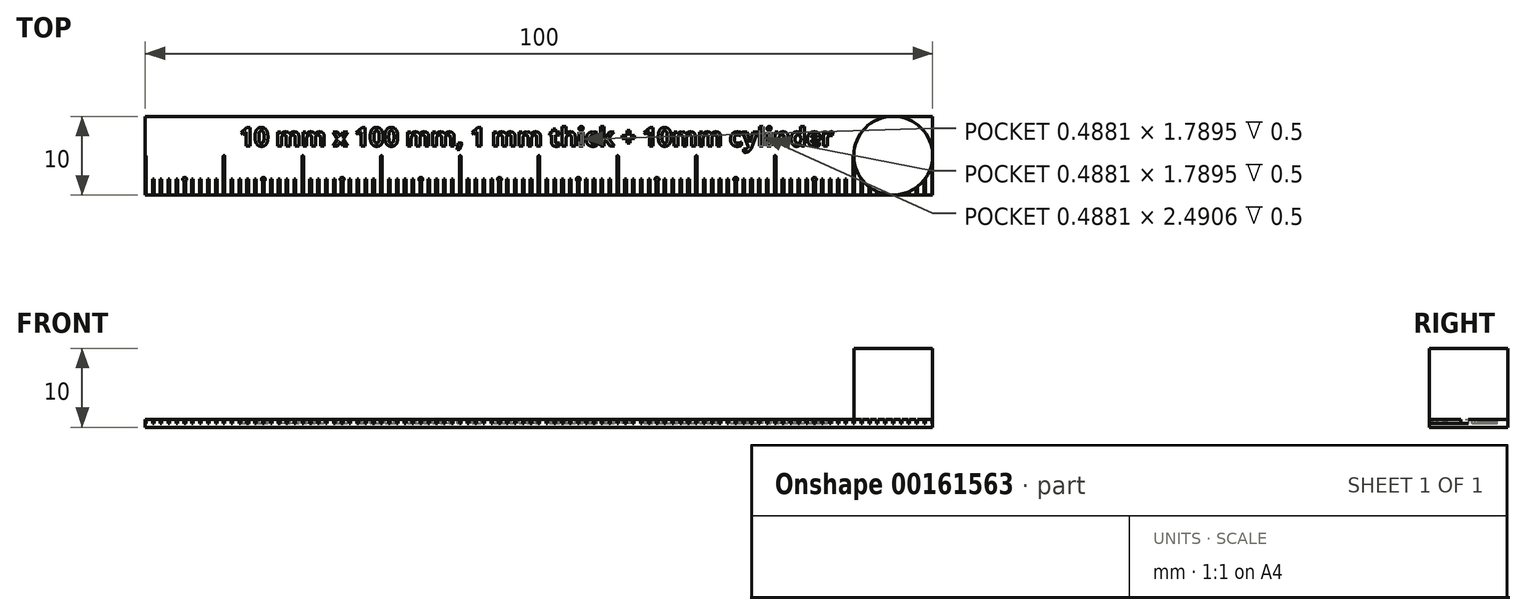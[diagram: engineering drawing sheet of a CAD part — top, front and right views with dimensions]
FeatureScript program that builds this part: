
annotation { "Feature Type Name" : "Feature", "Feature Type Description" : "" }
export const myFeature = defineFeature(function(context is Context, id is Id, definition is map)
    precondition{}
    {
        {
            var Q0;
            Q0=qCreatedBy(makeId("Top.planeOp"),FACE);
            var sketch = newSketch(context, id + "F0", { "sketchPlane" : qUnion([Q0])});
            skLineSegment(sketch, "E0.bottom", {"start": v(50, -5) * mm, "end": v(-50, -5) * mm});
            skLineSegment(sketch, "E0.top", {"start": v(50, 5) * mm, "end": v(-50, 5) * mm});
            skLineSegment(sketch, "E0.left", {"start": v(50, -5) * mm, "end": v(50, 5) * mm});
            skLineSegment(sketch, "E0.right", {"start": v(-50, -5) * mm, "end": v(-50, 5) * mm});
            skPoint(sketch, "E0.middle", {"position": v(0, 0) * mm});
            skSolve(sketch);
        }
        {
            var Q0;
            Q0=makeQuery(id+"F0.imprint","IMPRINT",FACE,{"disambiguationData":[TD([[makeQuery(id+"F0.imprint","IMPRINT",EDGE,{"derivedFrom":sQuery(id+"F0.wireOp",EDGE,"E0.bottom")}),-1.0]])]});
            extrude(context, id + "F1", {"entities" : qUnion([Q0]), "depth" : .5 * mm});
        }
        {
            var Q0;
            Q0=makeQuery(id+"F1.opExtrude","CAP_FACE",FACE,{"disambiguationData":[OSD([sQuery(id+"F0.wireOp",EDGE,"E0.bottom"),sQuery(id+"F0.wireOp",EDGE,"E0.top"),sQuery(id+"F0.wireOp",EDGE,"E0.left"),sQuery(id+"F0.wireOp",EDGE,"E0.right")])],"isStart":false});
            var sketch = newSketch(context, id + "F2", { "sketchPlane" : qUnion([Q0])});
            skLineSegment(sketch, "E1.bottom", {"start": v(-49.9, -5) * mm, "end": v(-50.1, -5) * mm});
            skLineSegment(sketch, "E1.top", {"start": v(-49.9, -0.1) * mm, "end": v(-50.1, -0.1) * mm});
            skLineSegment(sketch, "E1.left", {"start": v(-49.9, -5) * mm, "end": v(-49.9, -0.1) * mm});
            skLineSegment(sketch, "E1.right", {"start": v(-50.1, -5) * mm, "end": v(-50.1, -0.1) * mm});
            skPoint(sketch, "E1.middle", {"position": v(-50, -2.55) * mm});
            skArc(sketch, "E2", {"start": v(-49.9, -0.1) * mm, "mid": v(-50, 0) * mm, "end": v(-50.1, -0.1) * mm});
            skLineSegment(sketch, "E3.bottom", {"start": v(-49.1, -3) * mm, "end": v(-48.9, -3) * mm});
            skLineSegment(sketch, "E3.top", {"start": v(-49.1, -5) * mm, "end": v(-48.9, -5) * mm});
            skLineSegment(sketch, "E3.left", {"start": v(-49.1, -3) * mm, "end": v(-49.1, -5) * mm});
            skLineSegment(sketch, "E3.right", {"start": v(-48.9, -3) * mm, "end": v(-48.9, -5) * mm});
            skPoint(sketch, "E3.middle", {"position": v(-49, -4) * mm});
            skLineSegment(sketch, "E4.1.0.0", {"start": v(-48.1, -3) * mm, "end": v(-47.9, -3) * mm});
            skLineSegment(sketch, "E4.1.0.1", {"start": v(-48.1, -5) * mm, "end": v(-47.9, -5) * mm});
            skPoint(sketch, "E4.1.0.2", {"position": v(-48, -4) * mm});
            skLineSegment(sketch, "E4.1.0.3", {"start": v(-47.9, -3) * mm, "end": v(-47.9, -5) * mm});
            skLineSegment(sketch, "E4.1.0.4", {"start": v(-48.1, -3) * mm, "end": v(-48.1, -5) * mm});
            skLineSegment(sketch, "E4.2.0.0", {"start": v(-47.1, -3) * mm, "end": v(-46.9, -3) * mm});
            skLineSegment(sketch, "E4.2.0.1", {"start": v(-47.1, -5) * mm, "end": v(-46.9, -5) * mm});
            skPoint(sketch, "E4.2.0.2", {"position": v(-47, -4) * mm});
            skLineSegment(sketch, "E4.2.0.3", {"start": v(-46.9, -3) * mm, "end": v(-46.9, -5) * mm});
            skLineSegment(sketch, "E4.2.0.4", {"start": v(-47.1, -3) * mm, "end": v(-47.1, -5) * mm});
            skLineSegment(sketch, "E4.3.0.0", {"start": v(-46.1, -3) * mm, "end": v(-45.9, -3) * mm});
            skLineSegment(sketch, "E4.3.0.1", {"start": v(-46.1, -5) * mm, "end": v(-45.9, -5) * mm});
            skPoint(sketch, "E4.3.0.2", {"position": v(-46, -4) * mm});
            skLineSegment(sketch, "E4.3.0.3", {"start": v(-45.9, -3) * mm, "end": v(-45.9, -5) * mm});
            skLineSegment(sketch, "E4.3.0.4", {"start": v(-46.1, -3) * mm, "end": v(-46.1, -5) * mm});
            skLineSegment(sketch, "E4.4.0.0", {"start": v(-45.1, -3) * mm, "end": v(-44.9, -3) * mm});
            skLineSegment(sketch, "E4.4.0.1", {"start": v(-45.1, -5) * mm, "end": v(-44.9, -5) * mm});
            skPoint(sketch, "E4.4.0.2", {"position": v(-45, -4) * mm});
            skLineSegment(sketch, "E4.4.0.3", {"start": v(-44.9, -3) * mm, "end": v(-44.9, -5) * mm});
            skLineSegment(sketch, "E4.4.0.4", {"start": v(-45.1, -3) * mm, "end": v(-45.1, -5) * mm});
            skLineSegment(sketch, "E4.5.0.0", {"start": v(-44.1, -3) * mm, "end": v(-43.9, -3) * mm});
            skLineSegment(sketch, "E4.5.0.1", {"start": v(-44.1, -5) * mm, "end": v(-43.9, -5) * mm});
            skPoint(sketch, "E4.5.0.2", {"position": v(-44, -4) * mm});
            skLineSegment(sketch, "E4.5.0.3", {"start": v(-43.9, -3) * mm, "end": v(-43.9, -5) * mm});
            skLineSegment(sketch, "E4.5.0.4", {"start": v(-44.1, -3) * mm, "end": v(-44.1, -5) * mm});
            skLineSegment(sketch, "E4.6.0.0", {"start": v(-43.1, -3) * mm, "end": v(-42.9, -3) * mm});
            skLineSegment(sketch, "E4.6.0.1", {"start": v(-43.1, -5) * mm, "end": v(-42.9, -5) * mm});
            skPoint(sketch, "E4.6.0.2", {"position": v(-43, -4) * mm});
            skLineSegment(sketch, "E4.6.0.3", {"start": v(-42.9, -3) * mm, "end": v(-42.9, -5) * mm});
            skLineSegment(sketch, "E4.6.0.4", {"start": v(-43.1, -3) * mm, "end": v(-43.1, -5) * mm});
            skLineSegment(sketch, "E4.7.0.0", {"start": v(-42.1, -3) * mm, "end": v(-41.9, -3) * mm});
            skLineSegment(sketch, "E4.7.0.1", {"start": v(-42.1, -5) * mm, "end": v(-41.9, -5) * mm});
            skPoint(sketch, "E4.7.0.2", {"position": v(-42, -4) * mm});
            skLineSegment(sketch, "E4.7.0.3", {"start": v(-41.9, -3) * mm, "end": v(-41.9, -5) * mm});
            skLineSegment(sketch, "E4.7.0.4", {"start": v(-42.1, -3) * mm, "end": v(-42.1, -5) * mm});
            skLineSegment(sketch, "E4.8.0.0", {"start": v(-41.1, -3) * mm, "end": v(-40.9, -3) * mm});
            skLineSegment(sketch, "E4.8.0.1", {"start": v(-41.1, -5) * mm, "end": v(-40.9, -5) * mm});
            skPoint(sketch, "E4.8.0.2", {"position": v(-41, -4) * mm});
            skLineSegment(sketch, "E4.8.0.3", {"start": v(-40.9, -3) * mm, "end": v(-40.9, -5) * mm});
            skLineSegment(sketch, "E4.8.0.4", {"start": v(-41.1, -3) * mm, "end": v(-41.1, -5) * mm});
            skLineSegment(sketch, "E4.direction1", {"start": v(-49.1, -5) * mm, "end": v(-48.1, -5) * mm, "construction": true});
            skCircle(sketch, "E5", {"center": v(-45, -3) * mm, "radius": 0.25 * mm});
            skPoint(sketch, "E6.1.0.0", {"position": v(-36, -4) * mm});
            skPoint(sketch, "E6.1.0.1", {"position": v(-40, -2.55) * mm});
            skPoint(sketch, "E6.1.0.2", {"position": v(-35, -4) * mm});
            skLineSegment(sketch, "E6.1.0.3", {"start": v(-40.1, -5) * mm, "end": v(-40.1, -0.1) * mm});
            skPoint(sketch, "E6.1.0.4", {"position": v(-39, -4) * mm});
            skPoint(sketch, "E6.1.0.5", {"position": v(-37, -4) * mm});
            skPoint(sketch, "E6.1.0.6", {"position": v(-33, -4) * mm});
            skPoint(sketch, "E6.1.0.7", {"position": v(-31, -4) * mm});
            skPoint(sketch, "E6.1.0.8", {"position": v(-34, -4) * mm});
            skPoint(sketch, "E6.1.0.9", {"position": v(-38, -4) * mm});
            skPoint(sketch, "E6.1.0.10", {"position": v(-32, -4) * mm});
            skLineSegment(sketch, "E6.1.0.11", {"start": v(-32.9, -3) * mm, "end": v(-32.9, -5) * mm});
            skLineSegment(sketch, "E6.1.0.12", {"start": v(-35.9, -3) * mm, "end": v(-35.9, -5) * mm});
            skLineSegment(sketch, "E6.1.0.13", {"start": v(-31.9, -3) * mm, "end": v(-31.9, -5) * mm});
            skLineSegment(sketch, "E6.1.0.14", {"start": v(-38.1, -3) * mm, "end": v(-38.1, -5) * mm});
            skLineSegment(sketch, "E6.1.0.15", {"start": v(-37.9, -3) * mm, "end": v(-37.9, -5) * mm});
            skLineSegment(sketch, "E6.1.0.16", {"start": v(-38.9, -3) * mm, "end": v(-38.9, -5) * mm});
            skLineSegment(sketch, "E6.1.0.17", {"start": v(-39.1, -3) * mm, "end": v(-39.1, -5) * mm});
            skLineSegment(sketch, "E6.1.0.18", {"start": v(-39.9, -5) * mm, "end": v(-39.9, -0.1) * mm});
            skLineSegment(sketch, "E6.1.0.19", {"start": v(-36.9, -3) * mm, "end": v(-36.9, -5) * mm});
            skLineSegment(sketch, "E6.1.0.20", {"start": v(-34.1, -3) * mm, "end": v(-34.1, -5) * mm});
            skLineSegment(sketch, "E6.1.0.21", {"start": v(-31.1, -3) * mm, "end": v(-31.1, -5) * mm});
            skLineSegment(sketch, "E6.1.0.22", {"start": v(-35.1, -3) * mm, "end": v(-35.1, -5) * mm});
            skLineSegment(sketch, "E6.1.0.23", {"start": v(-37.1, -3) * mm, "end": v(-37.1, -5) * mm});
            skLineSegment(sketch, "E6.1.0.24", {"start": v(-33.1, -3) * mm, "end": v(-33.1, -5) * mm});
            skLineSegment(sketch, "E6.1.0.25", {"start": v(-36.1, -3) * mm, "end": v(-36.1, -5) * mm});
            skLineSegment(sketch, "E6.1.0.26", {"start": v(-32.1, -3) * mm, "end": v(-32.1, -5) * mm});
            skLineSegment(sketch, "E6.1.0.27", {"start": v(-34.9, -3) * mm, "end": v(-34.9, -5) * mm});
            skLineSegment(sketch, "E6.1.0.28", {"start": v(-30.9, -3) * mm, "end": v(-30.9, -5) * mm});
            skLineSegment(sketch, "E6.1.0.29", {"start": v(-33.9, -3) * mm, "end": v(-33.9, -5) * mm});
            skLineSegment(sketch, "E6.1.0.30", {"start": v(-38.1, -3) * mm, "end": v(-37.9, -3) * mm});
            skLineSegment(sketch, "E6.1.0.31", {"start": v(-39.1, -3) * mm, "end": v(-38.9, -3) * mm});
            skLineSegment(sketch, "E6.1.0.32", {"start": v(-36.1, -3) * mm, "end": v(-35.9, -3) * mm});
            skLineSegment(sketch, "E6.1.0.33", {"start": v(-32.1, -3) * mm, "end": v(-31.9, -3) * mm});
            skLineSegment(sketch, "E6.1.0.34", {"start": v(-31.1, -3) * mm, "end": v(-30.9, -3) * mm});
            skLineSegment(sketch, "E6.1.0.35", {"start": v(-31.1, -5) * mm, "end": v(-30.9, -5) * mm});
            skLineSegment(sketch, "E6.1.0.36", {"start": v(-32.1, -5) * mm, "end": v(-31.9, -5) * mm});
            skLineSegment(sketch, "E6.1.0.37", {"start": v(-35.1, -5) * mm, "end": v(-34.9, -5) * mm});
            skLineSegment(sketch, "E6.1.0.38", {"start": v(-36.1, -5) * mm, "end": v(-35.9, -5) * mm});
            skLineSegment(sketch, "E6.1.0.39", {"start": v(-34.1, -5) * mm, "end": v(-33.9, -5) * mm});
            skLineSegment(sketch, "E6.1.0.40", {"start": v(-34.1, -3) * mm, "end": v(-33.9, -3) * mm});
            skLineSegment(sketch, "E6.1.0.41", {"start": v(-39.9, -5) * mm, "end": v(-40.1, -5) * mm});
            skLineSegment(sketch, "E6.1.0.42", {"start": v(-37.1, -5) * mm, "end": v(-36.9, -5) * mm});
            skLineSegment(sketch, "E6.1.0.43", {"start": v(-37.1, -3) * mm, "end": v(-36.9, -3) * mm});
            skLineSegment(sketch, "E6.1.0.44", {"start": v(-33.1, -5) * mm, "end": v(-32.9, -5) * mm});
            skLineSegment(sketch, "E6.1.0.45", {"start": v(-33.1, -3) * mm, "end": v(-32.9, -3) * mm});
            skCircle(sketch, "E6.1.0.46", {"center": v(-35, -3) * mm, "radius": 0.25 * mm});
            skLineSegment(sketch, "E6.1.0.47", {"start": v(-39.1, -5) * mm, "end": v(-38.1, -5) * mm, "construction": true});
            skLineSegment(sketch, "E6.1.0.48", {"start": v(-38.1, -5) * mm, "end": v(-37.9, -5) * mm});
            skLineSegment(sketch, "E6.1.0.49", {"start": v(-39.1, -5) * mm, "end": v(-38.9, -5) * mm});
            skLineSegment(sketch, "E6.1.0.50", {"start": v(-35.1, -3) * mm, "end": v(-34.9, -3) * mm});
            skArc(sketch, "E6.1.0.51", {"start": v(-39.9, -0.1) * mm, "mid": v(-40, 0) * mm, "end": v(-40.1, -0.1) * mm});
            skLineSegment(sketch, "E6.1.0.52", {"start": v(-39.9, -0.1) * mm, "end": v(-40.1, -0.1) * mm});
            skPoint(sketch, "E6.2.0.0", {"position": v(-26, -4) * mm});
            skPoint(sketch, "E6.2.0.1", {"position": v(-30, -2.55) * mm});
            skPoint(sketch, "E6.2.0.2", {"position": v(-25, -4) * mm});
            skLineSegment(sketch, "E6.2.0.3", {"start": v(-30.1, -5) * mm, "end": v(-30.1, -0.1) * mm});
            skPoint(sketch, "E6.2.0.4", {"position": v(-29, -4) * mm});
            skPoint(sketch, "E6.2.0.5", {"position": v(-27, -4) * mm});
            skPoint(sketch, "E6.2.0.6", {"position": v(-23, -4) * mm});
            skPoint(sketch, "E6.2.0.7", {"position": v(-21, -4) * mm});
            skPoint(sketch, "E6.2.0.8", {"position": v(-24, -4) * mm});
            skPoint(sketch, "E6.2.0.9", {"position": v(-28, -4) * mm});
            skPoint(sketch, "E6.2.0.10", {"position": v(-22, -4) * mm});
            skLineSegment(sketch, "E6.2.0.11", {"start": v(-22.9, -3) * mm, "end": v(-22.9, -5) * mm});
            skLineSegment(sketch, "E6.2.0.12", {"start": v(-25.9, -3) * mm, "end": v(-25.9, -5) * mm});
            skLineSegment(sketch, "E6.2.0.13", {"start": v(-21.9, -3) * mm, "end": v(-21.9, -5) * mm});
            skLineSegment(sketch, "E6.2.0.14", {"start": v(-28.1, -3) * mm, "end": v(-28.1, -5) * mm});
            skLineSegment(sketch, "E6.2.0.15", {"start": v(-27.9, -3) * mm, "end": v(-27.9, -5) * mm});
            skLineSegment(sketch, "E6.2.0.16", {"start": v(-28.9, -3) * mm, "end": v(-28.9, -5) * mm});
            skLineSegment(sketch, "E6.2.0.17", {"start": v(-29.1, -3) * mm, "end": v(-29.1, -5) * mm});
            skLineSegment(sketch, "E6.2.0.18", {"start": v(-29.9, -5) * mm, "end": v(-29.9, -0.1) * mm});
            skLineSegment(sketch, "E6.2.0.19", {"start": v(-26.9, -3) * mm, "end": v(-26.9, -5) * mm});
            skLineSegment(sketch, "E6.2.0.20", {"start": v(-24.1, -3) * mm, "end": v(-24.1, -5) * mm});
            skLineSegment(sketch, "E6.2.0.21", {"start": v(-21.1, -3) * mm, "end": v(-21.1, -5) * mm});
            skLineSegment(sketch, "E6.2.0.22", {"start": v(-25.1, -3) * mm, "end": v(-25.1, -5) * mm});
            skLineSegment(sketch, "E6.2.0.23", {"start": v(-27.1, -3) * mm, "end": v(-27.1, -5) * mm});
            skLineSegment(sketch, "E6.2.0.24", {"start": v(-23.1, -3) * mm, "end": v(-23.1, -5) * mm});
            skLineSegment(sketch, "E6.2.0.25", {"start": v(-26.1, -3) * mm, "end": v(-26.1, -5) * mm});
            skLineSegment(sketch, "E6.2.0.26", {"start": v(-22.1, -3) * mm, "end": v(-22.1, -5) * mm});
            skLineSegment(sketch, "E6.2.0.27", {"start": v(-24.9, -3) * mm, "end": v(-24.9, -5) * mm});
            skLineSegment(sketch, "E6.2.0.28", {"start": v(-20.9, -3) * mm, "end": v(-20.9, -5) * mm});
            skLineSegment(sketch, "E6.2.0.29", {"start": v(-23.9, -3) * mm, "end": v(-23.9, -5) * mm});
            skLineSegment(sketch, "E6.2.0.30", {"start": v(-28.1, -3) * mm, "end": v(-27.9, -3) * mm});
            skLineSegment(sketch, "E6.2.0.31", {"start": v(-29.1, -3) * mm, "end": v(-28.9, -3) * mm});
            skLineSegment(sketch, "E6.2.0.32", {"start": v(-26.1, -3) * mm, "end": v(-25.9, -3) * mm});
            skLineSegment(sketch, "E6.2.0.33", {"start": v(-22.1, -3) * mm, "end": v(-21.9, -3) * mm});
            skLineSegment(sketch, "E6.2.0.34", {"start": v(-21.1, -3) * mm, "end": v(-20.9, -3) * mm});
            skLineSegment(sketch, "E6.2.0.35", {"start": v(-21.1, -5) * mm, "end": v(-20.9, -5) * mm});
            skLineSegment(sketch, "E6.2.0.36", {"start": v(-22.1, -5) * mm, "end": v(-21.9, -5) * mm});
            skLineSegment(sketch, "E6.2.0.37", {"start": v(-25.1, -5) * mm, "end": v(-24.9, -5) * mm});
            skLineSegment(sketch, "E6.2.0.38", {"start": v(-26.1, -5) * mm, "end": v(-25.9, -5) * mm});
            skLineSegment(sketch, "E6.2.0.39", {"start": v(-24.1, -5) * mm, "end": v(-23.9, -5) * mm});
            skLineSegment(sketch, "E6.2.0.40", {"start": v(-24.1, -3) * mm, "end": v(-23.9, -3) * mm});
            skLineSegment(sketch, "E6.2.0.41", {"start": v(-29.9, -5) * mm, "end": v(-30.1, -5) * mm});
            skLineSegment(sketch, "E6.2.0.42", {"start": v(-27.1, -5) * mm, "end": v(-26.9, -5) * mm});
            skLineSegment(sketch, "E6.2.0.43", {"start": v(-27.1, -3) * mm, "end": v(-26.9, -3) * mm});
            skLineSegment(sketch, "E6.2.0.44", {"start": v(-23.1, -5) * mm, "end": v(-22.9, -5) * mm});
            skLineSegment(sketch, "E6.2.0.45", {"start": v(-23.1, -3) * mm, "end": v(-22.9, -3) * mm});
            skCircle(sketch, "E6.2.0.46", {"center": v(-25, -3) * mm, "radius": 0.25 * mm});
            skLineSegment(sketch, "E6.2.0.47", {"start": v(-29.1, -5) * mm, "end": v(-28.1, -5) * mm, "construction": true});
            skLineSegment(sketch, "E6.2.0.48", {"start": v(-28.1, -5) * mm, "end": v(-27.9, -5) * mm});
            skLineSegment(sketch, "E6.2.0.49", {"start": v(-29.1, -5) * mm, "end": v(-28.9, -5) * mm});
            skLineSegment(sketch, "E6.2.0.50", {"start": v(-25.1, -3) * mm, "end": v(-24.9, -3) * mm});
            skArc(sketch, "E6.2.0.51", {"start": v(-29.9, -0.1) * mm, "mid": v(-30, 0) * mm, "end": v(-30.1, -0.1) * mm});
            skLineSegment(sketch, "E6.2.0.52", {"start": v(-29.9, -0.1) * mm, "end": v(-30.1, -0.1) * mm});
            skPoint(sketch, "E6.3.0.0", {"position": v(-16, -4) * mm});
            skPoint(sketch, "E6.3.0.1", {"position": v(-20, -2.55) * mm});
            skPoint(sketch, "E6.3.0.2", {"position": v(-15, -4) * mm});
            skLineSegment(sketch, "E6.3.0.3", {"start": v(-20.1, -5) * mm, "end": v(-20.1, -0.1) * mm});
            skPoint(sketch, "E6.3.0.4", {"position": v(-19, -4) * mm});
            skPoint(sketch, "E6.3.0.5", {"position": v(-17, -4) * mm});
            skPoint(sketch, "E6.3.0.6", {"position": v(-13, -4) * mm});
            skPoint(sketch, "E6.3.0.7", {"position": v(-11, -4) * mm});
            skPoint(sketch, "E6.3.0.8", {"position": v(-14, -4) * mm});
            skPoint(sketch, "E6.3.0.9", {"position": v(-18, -4) * mm});
            skPoint(sketch, "E6.3.0.10", {"position": v(-12, -4) * mm});
            skLineSegment(sketch, "E6.3.0.11", {"start": v(-12.9, -3) * mm, "end": v(-12.9, -5) * mm});
            skLineSegment(sketch, "E6.3.0.12", {"start": v(-15.9, -3) * mm, "end": v(-15.9, -5) * mm});
            skLineSegment(sketch, "E6.3.0.13", {"start": v(-11.9, -3) * mm, "end": v(-11.9, -5) * mm});
            skLineSegment(sketch, "E6.3.0.14", {"start": v(-18.1, -3) * mm, "end": v(-18.1, -5) * mm});
            skLineSegment(sketch, "E6.3.0.15", {"start": v(-17.9, -3) * mm, "end": v(-17.9, -5) * mm});
            skLineSegment(sketch, "E6.3.0.16", {"start": v(-18.9, -3) * mm, "end": v(-18.9, -5) * mm});
            skLineSegment(sketch, "E6.3.0.17", {"start": v(-19.1, -3) * mm, "end": v(-19.1, -5) * mm});
            skLineSegment(sketch, "E6.3.0.18", {"start": v(-19.9, -5) * mm, "end": v(-19.9, -0.1) * mm});
            skLineSegment(sketch, "E6.3.0.19", {"start": v(-16.9, -3) * mm, "end": v(-16.9, -5) * mm});
            skLineSegment(sketch, "E6.3.0.20", {"start": v(-14.1, -3) * mm, "end": v(-14.1, -5) * mm});
            skLineSegment(sketch, "E6.3.0.21", {"start": v(-11.1, -3) * mm, "end": v(-11.1, -5) * mm});
            skLineSegment(sketch, "E6.3.0.22", {"start": v(-15.1, -3) * mm, "end": v(-15.1, -5) * mm});
            skLineSegment(sketch, "E6.3.0.23", {"start": v(-17.1, -3) * mm, "end": v(-17.1, -5) * mm});
            skLineSegment(sketch, "E6.3.0.24", {"start": v(-13.1, -3) * mm, "end": v(-13.1, -5) * mm});
            skLineSegment(sketch, "E6.3.0.25", {"start": v(-16.1, -3) * mm, "end": v(-16.1, -5) * mm});
            skLineSegment(sketch, "E6.3.0.26", {"start": v(-12.1, -3) * mm, "end": v(-12.1, -5) * mm});
            skLineSegment(sketch, "E6.3.0.27", {"start": v(-14.9, -3) * mm, "end": v(-14.9, -5) * mm});
            skLineSegment(sketch, "E6.3.0.28", {"start": v(-10.9, -3) * mm, "end": v(-10.9, -5) * mm});
            skLineSegment(sketch, "E6.3.0.29", {"start": v(-13.9, -3) * mm, "end": v(-13.9, -5) * mm});
            skLineSegment(sketch, "E6.3.0.30", {"start": v(-18.1, -3) * mm, "end": v(-17.9, -3) * mm});
            skLineSegment(sketch, "E6.3.0.31", {"start": v(-19.1, -3) * mm, "end": v(-18.9, -3) * mm});
            skLineSegment(sketch, "E6.3.0.32", {"start": v(-16.1, -3) * mm, "end": v(-15.9, -3) * mm});
            skLineSegment(sketch, "E6.3.0.33", {"start": v(-12.1, -3) * mm, "end": v(-11.9, -3) * mm});
            skLineSegment(sketch, "E6.3.0.34", {"start": v(-11.1, -3) * mm, "end": v(-10.9, -3) * mm});
            skLineSegment(sketch, "E6.3.0.35", {"start": v(-11.1, -5) * mm, "end": v(-10.9, -5) * mm});
            skLineSegment(sketch, "E6.3.0.36", {"start": v(-12.1, -5) * mm, "end": v(-11.9, -5) * mm});
            skLineSegment(sketch, "E6.3.0.37", {"start": v(-15.1, -5) * mm, "end": v(-14.9, -5) * mm});
            skLineSegment(sketch, "E6.3.0.38", {"start": v(-16.1, -5) * mm, "end": v(-15.9, -5) * mm});
            skLineSegment(sketch, "E6.3.0.39", {"start": v(-14.1, -5) * mm, "end": v(-13.9, -5) * mm});
            skLineSegment(sketch, "E6.3.0.40", {"start": v(-14.1, -3) * mm, "end": v(-13.9, -3) * mm});
            skLineSegment(sketch, "E6.3.0.41", {"start": v(-19.9, -5) * mm, "end": v(-20.1, -5) * mm});
            skLineSegment(sketch, "E6.3.0.42", {"start": v(-17.1, -5) * mm, "end": v(-16.9, -5) * mm});
            skLineSegment(sketch, "E6.3.0.43", {"start": v(-17.1, -3) * mm, "end": v(-16.9, -3) * mm});
            skLineSegment(sketch, "E6.3.0.44", {"start": v(-13.1, -5) * mm, "end": v(-12.9, -5) * mm});
            skLineSegment(sketch, "E6.3.0.45", {"start": v(-13.1, -3) * mm, "end": v(-12.9, -3) * mm});
            skCircle(sketch, "E6.3.0.46", {"center": v(-15, -3) * mm, "radius": 0.25 * mm});
            skLineSegment(sketch, "E6.3.0.47", {"start": v(-19.1, -5) * mm, "end": v(-18.1, -5) * mm, "construction": true});
            skLineSegment(sketch, "E6.3.0.48", {"start": v(-18.1, -5) * mm, "end": v(-17.9, -5) * mm});
            skLineSegment(sketch, "E6.3.0.49", {"start": v(-19.1, -5) * mm, "end": v(-18.9, -5) * mm});
            skLineSegment(sketch, "E6.3.0.50", {"start": v(-15.1, -3) * mm, "end": v(-14.9, -3) * mm});
            skArc(sketch, "E6.3.0.51", {"start": v(-19.9, -0.1) * mm, "mid": v(-20, 0) * mm, "end": v(-20.1, -0.1) * mm});
            skLineSegment(sketch, "E6.3.0.52", {"start": v(-19.9, -0.1) * mm, "end": v(-20.1, -0.1) * mm});
            skPoint(sketch, "E6.4.0.0", {"position": v(-6, -4) * mm});
            skPoint(sketch, "E6.4.0.1", {"position": v(-10, -2.55) * mm});
            skPoint(sketch, "E6.4.0.2", {"position": v(-5, -4) * mm});
            skLineSegment(sketch, "E6.4.0.3", {"start": v(-10.1, -5) * mm, "end": v(-10.1, -0.1) * mm});
            skPoint(sketch, "E6.4.0.4", {"position": v(-9, -4) * mm});
            skPoint(sketch, "E6.4.0.5", {"position": v(-7, -4) * mm});
            skPoint(sketch, "E6.4.0.6", {"position": v(-3, -4) * mm});
            skPoint(sketch, "E6.4.0.7", {"position": v(-1, -4) * mm});
            skPoint(sketch, "E6.4.0.8", {"position": v(-4, -4) * mm});
            skPoint(sketch, "E6.4.0.9", {"position": v(-8, -4) * mm});
            skPoint(sketch, "E6.4.0.10", {"position": v(-2, -4) * mm});
            skLineSegment(sketch, "E6.4.0.11", {"start": v(-2.9, -3) * mm, "end": v(-2.9, -5) * mm});
            skLineSegment(sketch, "E6.4.0.12", {"start": v(-5.9, -3) * mm, "end": v(-5.9, -5) * mm});
            skLineSegment(sketch, "E6.4.0.13", {"start": v(-1.9, -3) * mm, "end": v(-1.9, -5) * mm});
            skLineSegment(sketch, "E6.4.0.14", {"start": v(-8.1, -3) * mm, "end": v(-8.1, -5) * mm});
            skLineSegment(sketch, "E6.4.0.15", {"start": v(-7.9, -3) * mm, "end": v(-7.9, -5) * mm});
            skLineSegment(sketch, "E6.4.0.16", {"start": v(-8.9, -3) * mm, "end": v(-8.9, -5) * mm});
            skLineSegment(sketch, "E6.4.0.17", {"start": v(-9.1, -3) * mm, "end": v(-9.1, -5) * mm});
            skLineSegment(sketch, "E6.4.0.18", {"start": v(-9.9, -5) * mm, "end": v(-9.9, -0.1) * mm});
            skLineSegment(sketch, "E6.4.0.19", {"start": v(-6.9, -3) * mm, "end": v(-6.9, -5) * mm});
            skLineSegment(sketch, "E6.4.0.20", {"start": v(-4.1, -3) * mm, "end": v(-4.1, -5) * mm});
            skLineSegment(sketch, "E6.4.0.21", {"start": v(-1.1, -3) * mm, "end": v(-1.1, -5) * mm});
            skLineSegment(sketch, "E6.4.0.22", {"start": v(-5.1, -3) * mm, "end": v(-5.1, -5) * mm});
            skLineSegment(sketch, "E6.4.0.23", {"start": v(-7.1, -3) * mm, "end": v(-7.1, -5) * mm});
            skLineSegment(sketch, "E6.4.0.24", {"start": v(-3.1, -3) * mm, "end": v(-3.1, -5) * mm});
            skLineSegment(sketch, "E6.4.0.25", {"start": v(-6.1, -3) * mm, "end": v(-6.1, -5) * mm});
            skLineSegment(sketch, "E6.4.0.26", {"start": v(-2.1, -3) * mm, "end": v(-2.1, -5) * mm});
            skLineSegment(sketch, "E6.4.0.27", {"start": v(-4.9, -3) * mm, "end": v(-4.9, -5) * mm});
            skLineSegment(sketch, "E6.4.0.28", {"start": v(-0.9, -3) * mm, "end": v(-0.9, -5) * mm});
            skLineSegment(sketch, "E6.4.0.29", {"start": v(-3.9, -3) * mm, "end": v(-3.9, -5) * mm});
            skLineSegment(sketch, "E6.4.0.30", {"start": v(-8.1, -3) * mm, "end": v(-7.9, -3) * mm});
            skLineSegment(sketch, "E6.4.0.31", {"start": v(-9.1, -3) * mm, "end": v(-8.9, -3) * mm});
            skLineSegment(sketch, "E6.4.0.32", {"start": v(-6.1, -3) * mm, "end": v(-5.9, -3) * mm});
            skLineSegment(sketch, "E6.4.0.33", {"start": v(-2.1, -3) * mm, "end": v(-1.9, -3) * mm});
            skLineSegment(sketch, "E6.4.0.34", {"start": v(-1.1, -3) * mm, "end": v(-0.9, -3) * mm});
            skLineSegment(sketch, "E6.4.0.35", {"start": v(-1.1, -5) * mm, "end": v(-0.9, -5) * mm});
            skLineSegment(sketch, "E6.4.0.36", {"start": v(-2.1, -5) * mm, "end": v(-1.9, -5) * mm});
            skLineSegment(sketch, "E6.4.0.37", {"start": v(-5.1, -5) * mm, "end": v(-4.9, -5) * mm});
            skLineSegment(sketch, "E6.4.0.38", {"start": v(-6.1, -5) * mm, "end": v(-5.9, -5) * mm});
            skLineSegment(sketch, "E6.4.0.39", {"start": v(-4.1, -5) * mm, "end": v(-3.9, -5) * mm});
            skLineSegment(sketch, "E6.4.0.40", {"start": v(-4.1, -3) * mm, "end": v(-3.9, -3) * mm});
            skLineSegment(sketch, "E6.4.0.41", {"start": v(-9.9, -5) * mm, "end": v(-10.1, -5) * mm});
            skLineSegment(sketch, "E6.4.0.42", {"start": v(-7.1, -5) * mm, "end": v(-6.9, -5) * mm});
            skLineSegment(sketch, "E6.4.0.43", {"start": v(-7.1, -3) * mm, "end": v(-6.9, -3) * mm});
            skLineSegment(sketch, "E6.4.0.44", {"start": v(-3.1, -5) * mm, "end": v(-2.9, -5) * mm});
            skLineSegment(sketch, "E6.4.0.45", {"start": v(-3.1, -3) * mm, "end": v(-2.9, -3) * mm});
            skCircle(sketch, "E6.4.0.46", {"center": v(-5, -3) * mm, "radius": 0.25 * mm});
            skLineSegment(sketch, "E6.4.0.47", {"start": v(-9.1, -5) * mm, "end": v(-8.1, -5) * mm, "construction": true});
            skLineSegment(sketch, "E6.4.0.48", {"start": v(-8.1, -5) * mm, "end": v(-7.9, -5) * mm});
            skLineSegment(sketch, "E6.4.0.49", {"start": v(-9.1, -5) * mm, "end": v(-8.9, -5) * mm});
            skLineSegment(sketch, "E6.4.0.50", {"start": v(-5.1, -3) * mm, "end": v(-4.9, -3) * mm});
            skArc(sketch, "E6.4.0.51", {"start": v(-9.9, -0.1) * mm, "mid": v(-10, 0) * mm, "end": v(-10.1, -0.1) * mm});
            skLineSegment(sketch, "E6.4.0.52", {"start": v(-9.9, -0.1) * mm, "end": v(-10.1, -0.1) * mm});
            skPoint(sketch, "E6.5.0.0", {"position": v(4, -4) * mm});
            skPoint(sketch, "E6.5.0.1", {"position": v(0, -2.55) * mm});
            skPoint(sketch, "E6.5.0.2", {"position": v(5, -4) * mm});
            skLineSegment(sketch, "E6.5.0.3", {"start": v(-0.1, -5) * mm, "end": v(-0.1, -0.1) * mm});
            skPoint(sketch, "E6.5.0.4", {"position": v(1, -4) * mm});
            skPoint(sketch, "E6.5.0.5", {"position": v(3, -4) * mm});
            skPoint(sketch, "E6.5.0.6", {"position": v(7, -4) * mm});
            skPoint(sketch, "E6.5.0.7", {"position": v(9, -4) * mm});
            skPoint(sketch, "E6.5.0.8", {"position": v(6, -4) * mm});
            skPoint(sketch, "E6.5.0.9", {"position": v(2, -4) * mm});
            skPoint(sketch, "E6.5.0.10", {"position": v(8, -4) * mm});
            skLineSegment(sketch, "E6.5.0.11", {"start": v(7.1, -3) * mm, "end": v(7.1, -5) * mm});
            skLineSegment(sketch, "E6.5.0.12", {"start": v(4.1, -3) * mm, "end": v(4.1, -5) * mm});
            skLineSegment(sketch, "E6.5.0.13", {"start": v(8.1, -3) * mm, "end": v(8.1, -5) * mm});
            skLineSegment(sketch, "E6.5.0.14", {"start": v(1.9, -3) * mm, "end": v(1.9, -5) * mm});
            skLineSegment(sketch, "E6.5.0.15", {"start": v(2.1, -3) * mm, "end": v(2.1, -5) * mm});
            skLineSegment(sketch, "E6.5.0.16", {"start": v(1.1, -3) * mm, "end": v(1.1, -5) * mm});
            skLineSegment(sketch, "E6.5.0.17", {"start": v(0.9, -3) * mm, "end": v(0.9, -5) * mm});
            skLineSegment(sketch, "E6.5.0.18", {"start": v(0.1, -5) * mm, "end": v(0.1, -0.1) * mm});
            skLineSegment(sketch, "E6.5.0.19", {"start": v(3.1, -3) * mm, "end": v(3.1, -5) * mm});
            skLineSegment(sketch, "E6.5.0.20", {"start": v(5.9, -3) * mm, "end": v(5.9, -5) * mm});
            skLineSegment(sketch, "E6.5.0.21", {"start": v(8.9, -3) * mm, "end": v(8.9, -5) * mm});
            skLineSegment(sketch, "E6.5.0.22", {"start": v(4.9, -3) * mm, "end": v(4.9, -5) * mm});
            skLineSegment(sketch, "E6.5.0.23", {"start": v(2.9, -3) * mm, "end": v(2.9, -5) * mm});
            skLineSegment(sketch, "E6.5.0.24", {"start": v(6.9, -3) * mm, "end": v(6.9, -5) * mm});
            skLineSegment(sketch, "E6.5.0.25", {"start": v(3.9, -3) * mm, "end": v(3.9, -5) * mm});
            skLineSegment(sketch, "E6.5.0.26", {"start": v(7.9, -3) * mm, "end": v(7.9, -5) * mm});
            skLineSegment(sketch, "E6.5.0.27", {"start": v(5.1, -3) * mm, "end": v(5.1, -5) * mm});
            skLineSegment(sketch, "E6.5.0.28", {"start": v(9.1, -3) * mm, "end": v(9.1, -5) * mm});
            skLineSegment(sketch, "E6.5.0.29", {"start": v(6.1, -3) * mm, "end": v(6.1, -5) * mm});
            skLineSegment(sketch, "E6.5.0.30", {"start": v(1.9, -3) * mm, "end": v(2.1, -3) * mm});
            skLineSegment(sketch, "E6.5.0.31", {"start": v(0.9, -3) * mm, "end": v(1.1, -3) * mm});
            skLineSegment(sketch, "E6.5.0.32", {"start": v(3.9, -3) * mm, "end": v(4.1, -3) * mm});
            skLineSegment(sketch, "E6.5.0.33", {"start": v(7.9, -3) * mm, "end": v(8.1, -3) * mm});
            skLineSegment(sketch, "E6.5.0.34", {"start": v(8.9, -3) * mm, "end": v(9.1, -3) * mm});
            skLineSegment(sketch, "E6.5.0.35", {"start": v(8.9, -5) * mm, "end": v(9.1, -5) * mm});
            skLineSegment(sketch, "E6.5.0.36", {"start": v(7.9, -5) * mm, "end": v(8.1, -5) * mm});
            skLineSegment(sketch, "E6.5.0.37", {"start": v(4.9, -5) * mm, "end": v(5.1, -5) * mm});
            skLineSegment(sketch, "E6.5.0.38", {"start": v(3.9, -5) * mm, "end": v(4.1, -5) * mm});
            skLineSegment(sketch, "E6.5.0.39", {"start": v(5.9, -5) * mm, "end": v(6.1, -5) * mm});
            skLineSegment(sketch, "E6.5.0.40", {"start": v(5.9, -3) * mm, "end": v(6.1, -3) * mm});
            skLineSegment(sketch, "E6.5.0.41", {"start": v(0.1, -5) * mm, "end": v(-0.1, -5) * mm});
            skLineSegment(sketch, "E6.5.0.42", {"start": v(2.9, -5) * mm, "end": v(3.1, -5) * mm});
            skLineSegment(sketch, "E6.5.0.43", {"start": v(2.9, -3) * mm, "end": v(3.1, -3) * mm});
            skLineSegment(sketch, "E6.5.0.44", {"start": v(6.9, -5) * mm, "end": v(7.1, -5) * mm});
            skLineSegment(sketch, "E6.5.0.45", {"start": v(6.9, -3) * mm, "end": v(7.1, -3) * mm});
            skCircle(sketch, "E6.5.0.46", {"center": v(5, -3) * mm, "radius": 0.25 * mm});
            skLineSegment(sketch, "E6.5.0.47", {"start": v(0.9, -5) * mm, "end": v(1.9, -5) * mm, "construction": true});
            skLineSegment(sketch, "E6.5.0.48", {"start": v(1.9, -5) * mm, "end": v(2.1, -5) * mm});
            skLineSegment(sketch, "E6.5.0.49", {"start": v(0.9, -5) * mm, "end": v(1.1, -5) * mm});
            skLineSegment(sketch, "E6.5.0.50", {"start": v(4.9, -3) * mm, "end": v(5.1, -3) * mm});
            skArc(sketch, "E6.5.0.51", {"start": v(0.1, -0.1) * mm, "mid": v(0, 0) * mm, "end": v(-0.1, -0.1) * mm});
            skLineSegment(sketch, "E6.5.0.52", {"start": v(0.1, -0.1) * mm, "end": v(-0.1, -0.1) * mm});
            skPoint(sketch, "E6.6.0.0", {"position": v(14, -4) * mm});
            skPoint(sketch, "E6.6.0.1", {"position": v(10, -2.55) * mm});
            skPoint(sketch, "E6.6.0.2", {"position": v(15, -4) * mm});
            skLineSegment(sketch, "E6.6.0.3", {"start": v(9.9, -5) * mm, "end": v(9.9, -0.1) * mm});
            skPoint(sketch, "E6.6.0.4", {"position": v(11, -4) * mm});
            skPoint(sketch, "E6.6.0.5", {"position": v(13, -4) * mm});
            skPoint(sketch, "E6.6.0.6", {"position": v(17, -4) * mm});
            skPoint(sketch, "E6.6.0.7", {"position": v(19, -4) * mm});
            skPoint(sketch, "E6.6.0.8", {"position": v(16, -4) * mm});
            skPoint(sketch, "E6.6.0.9", {"position": v(12, -4) * mm});
            skPoint(sketch, "E6.6.0.10", {"position": v(18, -4) * mm});
            skLineSegment(sketch, "E6.6.0.11", {"start": v(17.1, -3) * mm, "end": v(17.1, -5) * mm});
            skLineSegment(sketch, "E6.6.0.12", {"start": v(14.1, -3) * mm, "end": v(14.1, -5) * mm});
            skLineSegment(sketch, "E6.6.0.13", {"start": v(18.1, -3) * mm, "end": v(18.1, -5) * mm});
            skLineSegment(sketch, "E6.6.0.14", {"start": v(11.9, -3) * mm, "end": v(11.9, -5) * mm});
            skLineSegment(sketch, "E6.6.0.15", {"start": v(12.1, -3) * mm, "end": v(12.1, -5) * mm});
            skLineSegment(sketch, "E6.6.0.16", {"start": v(11.1, -3) * mm, "end": v(11.1, -5) * mm});
            skLineSegment(sketch, "E6.6.0.17", {"start": v(10.9, -3) * mm, "end": v(10.9, -5) * mm});
            skLineSegment(sketch, "E6.6.0.18", {"start": v(10.1, -5) * mm, "end": v(10.1, -0.1) * mm});
            skLineSegment(sketch, "E6.6.0.19", {"start": v(13.1, -3) * mm, "end": v(13.1, -5) * mm});
            skLineSegment(sketch, "E6.6.0.20", {"start": v(15.9, -3) * mm, "end": v(15.9, -5) * mm});
            skLineSegment(sketch, "E6.6.0.21", {"start": v(18.9, -3) * mm, "end": v(18.9, -5) * mm});
            skLineSegment(sketch, "E6.6.0.22", {"start": v(14.9, -3) * mm, "end": v(14.9, -5) * mm});
            skLineSegment(sketch, "E6.6.0.23", {"start": v(12.9, -3) * mm, "end": v(12.9, -5) * mm});
            skLineSegment(sketch, "E6.6.0.24", {"start": v(16.9, -3) * mm, "end": v(16.9, -5) * mm});
            skLineSegment(sketch, "E6.6.0.25", {"start": v(13.9, -3) * mm, "end": v(13.9, -5) * mm});
            skLineSegment(sketch, "E6.6.0.26", {"start": v(17.9, -3) * mm, "end": v(17.9, -5) * mm});
            skLineSegment(sketch, "E6.6.0.27", {"start": v(15.1, -3) * mm, "end": v(15.1, -5) * mm});
            skLineSegment(sketch, "E6.6.0.28", {"start": v(19.1, -3) * mm, "end": v(19.1, -5) * mm});
            skLineSegment(sketch, "E6.6.0.29", {"start": v(16.1, -3) * mm, "end": v(16.1, -5) * mm});
            skLineSegment(sketch, "E6.6.0.30", {"start": v(11.9, -3) * mm, "end": v(12.1, -3) * mm});
            skLineSegment(sketch, "E6.6.0.31", {"start": v(10.9, -3) * mm, "end": v(11.1, -3) * mm});
            skLineSegment(sketch, "E6.6.0.32", {"start": v(13.9, -3) * mm, "end": v(14.1, -3) * mm});
            skLineSegment(sketch, "E6.6.0.33", {"start": v(17.9, -3) * mm, "end": v(18.1, -3) * mm});
            skLineSegment(sketch, "E6.6.0.34", {"start": v(18.9, -3) * mm, "end": v(19.1, -3) * mm});
            skLineSegment(sketch, "E6.6.0.35", {"start": v(18.9, -5) * mm, "end": v(19.1, -5) * mm});
            skLineSegment(sketch, "E6.6.0.36", {"start": v(17.9, -5) * mm, "end": v(18.1, -5) * mm});
            skLineSegment(sketch, "E6.6.0.37", {"start": v(14.9, -5) * mm, "end": v(15.1, -5) * mm});
            skLineSegment(sketch, "E6.6.0.38", {"start": v(13.9, -5) * mm, "end": v(14.1, -5) * mm});
            skLineSegment(sketch, "E6.6.0.39", {"start": v(15.9, -5) * mm, "end": v(16.1, -5) * mm});
            skLineSegment(sketch, "E6.6.0.40", {"start": v(15.9, -3) * mm, "end": v(16.1, -3) * mm});
            skLineSegment(sketch, "E6.6.0.41", {"start": v(10.1, -5) * mm, "end": v(9.9, -5) * mm});
            skLineSegment(sketch, "E6.6.0.42", {"start": v(12.9, -5) * mm, "end": v(13.1, -5) * mm});
            skLineSegment(sketch, "E6.6.0.43", {"start": v(12.9, -3) * mm, "end": v(13.1, -3) * mm});
            skLineSegment(sketch, "E6.6.0.44", {"start": v(16.9, -5) * mm, "end": v(17.1, -5) * mm});
            skLineSegment(sketch, "E6.6.0.45", {"start": v(16.9, -3) * mm, "end": v(17.1, -3) * mm});
            skCircle(sketch, "E6.6.0.46", {"center": v(15, -3) * mm, "radius": 0.25 * mm});
            skLineSegment(sketch, "E6.6.0.47", {"start": v(10.9, -5) * mm, "end": v(11.9, -5) * mm, "construction": true});
            skLineSegment(sketch, "E6.6.0.48", {"start": v(11.9, -5) * mm, "end": v(12.1, -5) * mm});
            skLineSegment(sketch, "E6.6.0.49", {"start": v(10.9, -5) * mm, "end": v(11.1, -5) * mm});
            skLineSegment(sketch, "E6.6.0.50", {"start": v(14.9, -3) * mm, "end": v(15.1, -3) * mm});
            skArc(sketch, "E6.6.0.51", {"start": v(10.1, -0.1) * mm, "mid": v(10, 0) * mm, "end": v(9.9, -0.1) * mm});
            skLineSegment(sketch, "E6.6.0.52", {"start": v(10.1, -0.1) * mm, "end": v(9.9, -0.1) * mm});
            skPoint(sketch, "E6.7.0.0", {"position": v(24, -4) * mm});
            skPoint(sketch, "E6.7.0.1", {"position": v(20, -2.55) * mm});
            skPoint(sketch, "E6.7.0.2", {"position": v(25, -4) * mm});
            skLineSegment(sketch, "E6.7.0.3", {"start": v(19.9, -5) * mm, "end": v(19.9, -0.1) * mm});
            skPoint(sketch, "E6.7.0.4", {"position": v(21, -4) * mm});
            skPoint(sketch, "E6.7.0.5", {"position": v(23, -4) * mm});
            skPoint(sketch, "E6.7.0.6", {"position": v(27, -4) * mm});
            skPoint(sketch, "E6.7.0.7", {"position": v(29, -4) * mm});
            skPoint(sketch, "E6.7.0.8", {"position": v(26, -4) * mm});
            skPoint(sketch, "E6.7.0.9", {"position": v(22, -4) * mm});
            skPoint(sketch, "E6.7.0.10", {"position": v(28, -4) * mm});
            skLineSegment(sketch, "E6.7.0.11", {"start": v(27.1, -3) * mm, "end": v(27.1, -5) * mm});
            skLineSegment(sketch, "E6.7.0.12", {"start": v(24.1, -3) * mm, "end": v(24.1, -5) * mm});
            skLineSegment(sketch, "E6.7.0.13", {"start": v(28.1, -3) * mm, "end": v(28.1, -5) * mm});
            skLineSegment(sketch, "E6.7.0.14", {"start": v(21.9, -3) * mm, "end": v(21.9, -5) * mm});
            skLineSegment(sketch, "E6.7.0.15", {"start": v(22.1, -3) * mm, "end": v(22.1, -5) * mm});
            skLineSegment(sketch, "E6.7.0.16", {"start": v(21.1, -3) * mm, "end": v(21.1, -5) * mm});
            skLineSegment(sketch, "E6.7.0.17", {"start": v(20.9, -3) * mm, "end": v(20.9, -5) * mm});
            skLineSegment(sketch, "E6.7.0.18", {"start": v(20.1, -5) * mm, "end": v(20.1, -0.1) * mm});
            skLineSegment(sketch, "E6.7.0.19", {"start": v(23.1, -3) * mm, "end": v(23.1, -5) * mm});
            skLineSegment(sketch, "E6.7.0.20", {"start": v(25.9, -3) * mm, "end": v(25.9, -5) * mm});
            skLineSegment(sketch, "E6.7.0.21", {"start": v(28.9, -3) * mm, "end": v(28.9, -5) * mm});
            skLineSegment(sketch, "E6.7.0.22", {"start": v(24.9, -3) * mm, "end": v(24.9, -5) * mm});
            skLineSegment(sketch, "E6.7.0.23", {"start": v(22.9, -3) * mm, "end": v(22.9, -5) * mm});
            skLineSegment(sketch, "E6.7.0.24", {"start": v(26.9, -3) * mm, "end": v(26.9, -5) * mm});
            skLineSegment(sketch, "E6.7.0.25", {"start": v(23.9, -3) * mm, "end": v(23.9, -5) * mm});
            skLineSegment(sketch, "E6.7.0.26", {"start": v(27.9, -3) * mm, "end": v(27.9, -5) * mm});
            skLineSegment(sketch, "E6.7.0.27", {"start": v(25.1, -3) * mm, "end": v(25.1, -5) * mm});
            skLineSegment(sketch, "E6.7.0.28", {"start": v(29.1, -3) * mm, "end": v(29.1, -5) * mm});
            skLineSegment(sketch, "E6.7.0.29", {"start": v(26.1, -3) * mm, "end": v(26.1, -5) * mm});
            skLineSegment(sketch, "E6.7.0.30", {"start": v(21.9, -3) * mm, "end": v(22.1, -3) * mm});
            skLineSegment(sketch, "E6.7.0.31", {"start": v(20.9, -3) * mm, "end": v(21.1, -3) * mm});
            skLineSegment(sketch, "E6.7.0.32", {"start": v(23.9, -3) * mm, "end": v(24.1, -3) * mm});
            skLineSegment(sketch, "E6.7.0.33", {"start": v(27.9, -3) * mm, "end": v(28.1, -3) * mm});
            skLineSegment(sketch, "E6.7.0.34", {"start": v(28.9, -3) * mm, "end": v(29.1, -3) * mm});
            skLineSegment(sketch, "E6.7.0.35", {"start": v(28.9, -5) * mm, "end": v(29.1, -5) * mm});
            skLineSegment(sketch, "E6.7.0.36", {"start": v(27.9, -5) * mm, "end": v(28.1, -5) * mm});
            skLineSegment(sketch, "E6.7.0.37", {"start": v(24.9, -5) * mm, "end": v(25.1, -5) * mm});
            skLineSegment(sketch, "E6.7.0.38", {"start": v(23.9, -5) * mm, "end": v(24.1, -5) * mm});
            skLineSegment(sketch, "E6.7.0.39", {"start": v(25.9, -5) * mm, "end": v(26.1, -5) * mm});
            skLineSegment(sketch, "E6.7.0.40", {"start": v(25.9, -3) * mm, "end": v(26.1, -3) * mm});
            skLineSegment(sketch, "E6.7.0.41", {"start": v(20.1, -5) * mm, "end": v(19.9, -5) * mm});
            skLineSegment(sketch, "E6.7.0.42", {"start": v(22.9, -5) * mm, "end": v(23.1, -5) * mm});
            skLineSegment(sketch, "E6.7.0.43", {"start": v(22.9, -3) * mm, "end": v(23.1, -3) * mm});
            skLineSegment(sketch, "E6.7.0.44", {"start": v(26.9, -5) * mm, "end": v(27.1, -5) * mm});
            skLineSegment(sketch, "E6.7.0.45", {"start": v(26.9, -3) * mm, "end": v(27.1, -3) * mm});
            skCircle(sketch, "E6.7.0.46", {"center": v(25, -3) * mm, "radius": 0.25 * mm});
            skLineSegment(sketch, "E6.7.0.47", {"start": v(20.9, -5) * mm, "end": v(21.9, -5) * mm, "construction": true});
            skLineSegment(sketch, "E6.7.0.48", {"start": v(21.9, -5) * mm, "end": v(22.1, -5) * mm});
            skLineSegment(sketch, "E6.7.0.49", {"start": v(20.9, -5) * mm, "end": v(21.1, -5) * mm});
            skLineSegment(sketch, "E6.7.0.50", {"start": v(24.9, -3) * mm, "end": v(25.1, -3) * mm});
            skArc(sketch, "E6.7.0.51", {"start": v(20.1, -0.1) * mm, "mid": v(20, 0) * mm, "end": v(19.9, -0.1) * mm});
            skLineSegment(sketch, "E6.7.0.52", {"start": v(20.1, -0.1) * mm, "end": v(19.9, -0.1) * mm});
            skPoint(sketch, "E6.8.0.0", {"position": v(34, -4) * mm});
            skPoint(sketch, "E6.8.0.1", {"position": v(30, -2.55) * mm});
            skPoint(sketch, "E6.8.0.2", {"position": v(35, -4) * mm});
            skLineSegment(sketch, "E6.8.0.3", {"start": v(29.9, -5) * mm, "end": v(29.9, -0.1) * mm});
            skPoint(sketch, "E6.8.0.4", {"position": v(31, -4) * mm});
            skPoint(sketch, "E6.8.0.5", {"position": v(33, -4) * mm});
            skPoint(sketch, "E6.8.0.6", {"position": v(37, -4) * mm});
            skPoint(sketch, "E6.8.0.7", {"position": v(39, -4) * mm});
            skPoint(sketch, "E6.8.0.8", {"position": v(36, -4) * mm});
            skPoint(sketch, "E6.8.0.9", {"position": v(32, -4) * mm});
            skPoint(sketch, "E6.8.0.10", {"position": v(38, -4) * mm});
            skLineSegment(sketch, "E6.8.0.11", {"start": v(37.1, -3) * mm, "end": v(37.1, -5) * mm});
            skLineSegment(sketch, "E6.8.0.12", {"start": v(34.1, -3) * mm, "end": v(34.1, -5) * mm});
            skLineSegment(sketch, "E6.8.0.13", {"start": v(38.1, -3) * mm, "end": v(38.1, -5) * mm});
            skLineSegment(sketch, "E6.8.0.14", {"start": v(31.9, -3) * mm, "end": v(31.9, -5) * mm});
            skLineSegment(sketch, "E6.8.0.15", {"start": v(32.1, -3) * mm, "end": v(32.1, -5) * mm});
            skLineSegment(sketch, "E6.8.0.16", {"start": v(31.1, -3) * mm, "end": v(31.1, -5) * mm});
            skLineSegment(sketch, "E6.8.0.17", {"start": v(30.9, -3) * mm, "end": v(30.9, -5) * mm});
            skLineSegment(sketch, "E6.8.0.18", {"start": v(30.1, -5) * mm, "end": v(30.1, -0.1) * mm});
            skLineSegment(sketch, "E6.8.0.19", {"start": v(33.1, -3) * mm, "end": v(33.1, -5) * mm});
            skLineSegment(sketch, "E6.8.0.20", {"start": v(35.9, -3) * mm, "end": v(35.9, -5) * mm});
            skLineSegment(sketch, "E6.8.0.21", {"start": v(38.9, -3) * mm, "end": v(38.9, -5) * mm});
            skLineSegment(sketch, "E6.8.0.22", {"start": v(34.9, -3) * mm, "end": v(34.9, -5) * mm});
            skLineSegment(sketch, "E6.8.0.23", {"start": v(32.9, -3) * mm, "end": v(32.9, -5) * mm});
            skLineSegment(sketch, "E6.8.0.24", {"start": v(36.9, -3) * mm, "end": v(36.9, -5) * mm});
            skLineSegment(sketch, "E6.8.0.25", {"start": v(33.9, -3) * mm, "end": v(33.9, -5) * mm});
            skLineSegment(sketch, "E6.8.0.26", {"start": v(37.9, -3) * mm, "end": v(37.9, -5) * mm});
            skLineSegment(sketch, "E6.8.0.27", {"start": v(35.1, -3) * mm, "end": v(35.1, -5) * mm});
            skLineSegment(sketch, "E6.8.0.28", {"start": v(39.1, -3) * mm, "end": v(39.1, -5) * mm});
            skLineSegment(sketch, "E6.8.0.29", {"start": v(36.1, -3) * mm, "end": v(36.1, -5) * mm});
            skLineSegment(sketch, "E6.8.0.30", {"start": v(31.9, -3) * mm, "end": v(32.1, -3) * mm});
            skLineSegment(sketch, "E6.8.0.31", {"start": v(30.9, -3) * mm, "end": v(31.1, -3) * mm});
            skLineSegment(sketch, "E6.8.0.32", {"start": v(33.9, -3) * mm, "end": v(34.1, -3) * mm});
            skLineSegment(sketch, "E6.8.0.33", {"start": v(37.9, -3) * mm, "end": v(38.1, -3) * mm});
            skLineSegment(sketch, "E6.8.0.34", {"start": v(38.9, -3) * mm, "end": v(39.1, -3) * mm});
            skLineSegment(sketch, "E6.8.0.35", {"start": v(38.9, -5) * mm, "end": v(39.1, -5) * mm});
            skLineSegment(sketch, "E6.8.0.36", {"start": v(37.9, -5) * mm, "end": v(38.1, -5) * mm});
            skLineSegment(sketch, "E6.8.0.37", {"start": v(34.9, -5) * mm, "end": v(35.1, -5) * mm});
            skLineSegment(sketch, "E6.8.0.38", {"start": v(33.9, -5) * mm, "end": v(34.1, -5) * mm});
            skLineSegment(sketch, "E6.8.0.39", {"start": v(35.9, -5) * mm, "end": v(36.1, -5) * mm});
            skLineSegment(sketch, "E6.8.0.40", {"start": v(35.9, -3) * mm, "end": v(36.1, -3) * mm});
            skLineSegment(sketch, "E6.8.0.41", {"start": v(30.1, -5) * mm, "end": v(29.9, -5) * mm});
            skLineSegment(sketch, "E6.8.0.42", {"start": v(32.9, -5) * mm, "end": v(33.1, -5) * mm});
            skLineSegment(sketch, "E6.8.0.43", {"start": v(32.9, -3) * mm, "end": v(33.1, -3) * mm});
            skLineSegment(sketch, "E6.8.0.44", {"start": v(36.9, -5) * mm, "end": v(37.1, -5) * mm});
            skLineSegment(sketch, "E6.8.0.45", {"start": v(36.9, -3) * mm, "end": v(37.1, -3) * mm});
            skCircle(sketch, "E6.8.0.46", {"center": v(35, -3) * mm, "radius": 0.25 * mm});
            skLineSegment(sketch, "E6.8.0.47", {"start": v(30.9, -5) * mm, "end": v(31.9, -5) * mm, "construction": true});
            skLineSegment(sketch, "E6.8.0.48", {"start": v(31.9, -5) * mm, "end": v(32.1, -5) * mm});
            skLineSegment(sketch, "E6.8.0.49", {"start": v(30.9, -5) * mm, "end": v(31.1, -5) * mm});
            skLineSegment(sketch, "E6.8.0.50", {"start": v(34.9, -3) * mm, "end": v(35.1, -3) * mm});
            skArc(sketch, "E6.8.0.51", {"start": v(30.1, -0.1) * mm, "mid": v(30, 0) * mm, "end": v(29.9, -0.1) * mm});
            skLineSegment(sketch, "E6.8.0.52", {"start": v(30.1, -0.1) * mm, "end": v(29.9, -0.1) * mm});
            skPoint(sketch, "E6.9.0.0", {"position": v(44, -4) * mm});
            skPoint(sketch, "E6.9.0.1", {"position": v(40, -2.55) * mm});
            skPoint(sketch, "E6.9.0.2", {"position": v(45, -4) * mm});
            skLineSegment(sketch, "E6.9.0.3", {"start": v(39.9, -5) * mm, "end": v(39.9, -0.1) * mm});
            skPoint(sketch, "E6.9.0.4", {"position": v(41, -4) * mm});
            skPoint(sketch, "E6.9.0.5", {"position": v(43, -4) * mm});
            skPoint(sketch, "E6.9.0.6", {"position": v(47, -4) * mm});
            skPoint(sketch, "E6.9.0.7", {"position": v(49, -4) * mm});
            skPoint(sketch, "E6.9.0.8", {"position": v(46, -4) * mm});
            skPoint(sketch, "E6.9.0.9", {"position": v(42, -4) * mm});
            skPoint(sketch, "E6.9.0.10", {"position": v(48, -4) * mm});
            skLineSegment(sketch, "E6.9.0.11", {"start": v(47.1, -3) * mm, "end": v(47.1, -5) * mm});
            skLineSegment(sketch, "E6.9.0.12", {"start": v(44.1, -3) * mm, "end": v(44.1, -5) * mm});
            skLineSegment(sketch, "E6.9.0.13", {"start": v(48.1, -3) * mm, "end": v(48.1, -5) * mm});
            skLineSegment(sketch, "E6.9.0.14", {"start": v(41.9, -3) * mm, "end": v(41.9, -5) * mm});
            skLineSegment(sketch, "E6.9.0.15", {"start": v(42.1, -3) * mm, "end": v(42.1, -5) * mm});
            skLineSegment(sketch, "E6.9.0.16", {"start": v(41.1, -3) * mm, "end": v(41.1, -5) * mm});
            skLineSegment(sketch, "E6.9.0.17", {"start": v(40.9, -3) * mm, "end": v(40.9, -5) * mm});
            skLineSegment(sketch, "E6.9.0.18", {"start": v(40.1, -5) * mm, "end": v(40.1, -0.1) * mm});
            skLineSegment(sketch, "E6.9.0.19", {"start": v(43.1, -3) * mm, "end": v(43.1, -5) * mm});
            skLineSegment(sketch, "E6.9.0.20", {"start": v(45.9, -3) * mm, "end": v(45.9, -5) * mm});
            skLineSegment(sketch, "E6.9.0.21", {"start": v(48.9, -3) * mm, "end": v(48.9, -5) * mm});
            skLineSegment(sketch, "E6.9.0.22", {"start": v(44.9, -3) * mm, "end": v(44.9, -5) * mm});
            skLineSegment(sketch, "E6.9.0.23", {"start": v(42.9, -3) * mm, "end": v(42.9, -5) * mm});
            skLineSegment(sketch, "E6.9.0.24", {"start": v(46.9, -3) * mm, "end": v(46.9, -5) * mm});
            skLineSegment(sketch, "E6.9.0.25", {"start": v(43.9, -3) * mm, "end": v(43.9, -5) * mm});
            skLineSegment(sketch, "E6.9.0.26", {"start": v(47.9, -3) * mm, "end": v(47.9, -5) * mm});
            skLineSegment(sketch, "E6.9.0.27", {"start": v(45.1, -3) * mm, "end": v(45.1, -5) * mm});
            skLineSegment(sketch, "E6.9.0.28", {"start": v(49.1, -3) * mm, "end": v(49.1, -5) * mm});
            skLineSegment(sketch, "E6.9.0.29", {"start": v(46.1, -3) * mm, "end": v(46.1, -5) * mm});
            skLineSegment(sketch, "E6.9.0.30", {"start": v(41.9, -3) * mm, "end": v(42.1, -3) * mm});
            skLineSegment(sketch, "E6.9.0.31", {"start": v(40.9, -3) * mm, "end": v(41.1, -3) * mm});
            skLineSegment(sketch, "E6.9.0.32", {"start": v(43.9, -3) * mm, "end": v(44.1, -3) * mm});
            skLineSegment(sketch, "E6.9.0.33", {"start": v(47.9, -3) * mm, "end": v(48.1, -3) * mm});
            skLineSegment(sketch, "E6.9.0.34", {"start": v(48.9, -3) * mm, "end": v(49.1, -3) * mm});
            skLineSegment(sketch, "E6.9.0.35", {"start": v(48.9, -5) * mm, "end": v(49.1, -5) * mm});
            skLineSegment(sketch, "E6.9.0.36", {"start": v(47.9, -5) * mm, "end": v(48.1, -5) * mm});
            skLineSegment(sketch, "E6.9.0.37", {"start": v(44.9, -5) * mm, "end": v(45.1, -5) * mm});
            skLineSegment(sketch, "E6.9.0.38", {"start": v(43.9, -5) * mm, "end": v(44.1, -5) * mm});
            skLineSegment(sketch, "E6.9.0.39", {"start": v(45.9, -5) * mm, "end": v(46.1, -5) * mm});
            skLineSegment(sketch, "E6.9.0.40", {"start": v(45.9, -3) * mm, "end": v(46.1, -3) * mm});
            skLineSegment(sketch, "E6.9.0.41", {"start": v(40.1, -5) * mm, "end": v(39.9, -5) * mm});
            skLineSegment(sketch, "E6.9.0.42", {"start": v(42.9, -5) * mm, "end": v(43.1, -5) * mm});
            skLineSegment(sketch, "E6.9.0.43", {"start": v(42.9, -3) * mm, "end": v(43.1, -3) * mm});
            skLineSegment(sketch, "E6.9.0.44", {"start": v(46.9, -5) * mm, "end": v(47.1, -5) * mm});
            skLineSegment(sketch, "E6.9.0.45", {"start": v(46.9, -3) * mm, "end": v(47.1, -3) * mm});
            skCircle(sketch, "E6.9.0.46", {"center": v(45, -3) * mm, "radius": 0.25 * mm});
            skLineSegment(sketch, "E6.9.0.47", {"start": v(40.9, -5) * mm, "end": v(41.9, -5) * mm, "construction": true});
            skLineSegment(sketch, "E6.9.0.48", {"start": v(41.9, -5) * mm, "end": v(42.1, -5) * mm});
            skLineSegment(sketch, "E6.9.0.49", {"start": v(40.9, -5) * mm, "end": v(41.1, -5) * mm});
            skLineSegment(sketch, "E6.9.0.50", {"start": v(44.9, -3) * mm, "end": v(45.1, -3) * mm});
            skArc(sketch, "E6.9.0.51", {"start": v(40.1, -0.1) * mm, "mid": v(40, 0) * mm, "end": v(39.9, -0.1) * mm});
            skLineSegment(sketch, "E6.9.0.52", {"start": v(40.1, -0.1) * mm, "end": v(39.9, -0.1) * mm});
            skPoint(sketch, "E6.10.0.0", {"position": v(54, -4) * mm});
            skPoint(sketch, "E6.10.0.1", {"position": v(50, -2.55) * mm});
            skPoint(sketch, "E6.10.0.2", {"position": v(55, -4) * mm});
            skLineSegment(sketch, "E6.10.0.3", {"start": v(49.9, -5) * mm, "end": v(49.9, -0.1) * mm});
            skPoint(sketch, "E6.10.0.4", {"position": v(51, -4) * mm});
            skPoint(sketch, "E6.10.0.5", {"position": v(53, -4) * mm});
            skPoint(sketch, "E6.10.0.6", {"position": v(57, -4) * mm});
            skPoint(sketch, "E6.10.0.7", {"position": v(59, -4) * mm});
            skPoint(sketch, "E6.10.0.8", {"position": v(56, -4) * mm});
            skPoint(sketch, "E6.10.0.9", {"position": v(52, -4) * mm});
            skPoint(sketch, "E6.10.0.10", {"position": v(58, -4) * mm});
            skLineSegment(sketch, "E6.10.0.11", {"start": v(57.1, -3) * mm, "end": v(57.1, -5) * mm});
            skLineSegment(sketch, "E6.10.0.12", {"start": v(54.1, -3) * mm, "end": v(54.1, -5) * mm});
            skLineSegment(sketch, "E6.10.0.13", {"start": v(58.1, -3) * mm, "end": v(58.1, -5) * mm});
            skLineSegment(sketch, "E6.10.0.14", {"start": v(51.9, -3) * mm, "end": v(51.9, -5) * mm});
            skLineSegment(sketch, "E6.10.0.15", {"start": v(52.1, -3) * mm, "end": v(52.1, -5) * mm});
            skLineSegment(sketch, "E6.10.0.16", {"start": v(51.1, -3) * mm, "end": v(51.1, -5) * mm});
            skLineSegment(sketch, "E6.10.0.17", {"start": v(50.9, -3) * mm, "end": v(50.9, -5) * mm});
            skLineSegment(sketch, "E6.10.0.18", {"start": v(50.1, -5) * mm, "end": v(50.1, -0.1) * mm});
            skLineSegment(sketch, "E6.10.0.19", {"start": v(53.1, -3) * mm, "end": v(53.1, -5) * mm});
            skLineSegment(sketch, "E6.10.0.20", {"start": v(55.9, -3) * mm, "end": v(55.9, -5) * mm});
            skLineSegment(sketch, "E6.10.0.21", {"start": v(58.9, -3) * mm, "end": v(58.9, -5) * mm});
            skLineSegment(sketch, "E6.10.0.22", {"start": v(54.9, -3) * mm, "end": v(54.9, -5) * mm});
            skLineSegment(sketch, "E6.10.0.23", {"start": v(52.9, -3) * mm, "end": v(52.9, -5) * mm});
            skLineSegment(sketch, "E6.10.0.24", {"start": v(56.9, -3) * mm, "end": v(56.9, -5) * mm});
            skLineSegment(sketch, "E6.10.0.25", {"start": v(53.9, -3) * mm, "end": v(53.9, -5) * mm});
            skLineSegment(sketch, "E6.10.0.26", {"start": v(57.9, -3) * mm, "end": v(57.9, -5) * mm});
            skLineSegment(sketch, "E6.10.0.27", {"start": v(55.1, -3) * mm, "end": v(55.1, -5) * mm});
            skLineSegment(sketch, "E6.10.0.28", {"start": v(59.1, -3) * mm, "end": v(59.1, -5) * mm});
            skLineSegment(sketch, "E6.10.0.29", {"start": v(56.1, -3) * mm, "end": v(56.1, -5) * mm});
            skLineSegment(sketch, "E6.10.0.30", {"start": v(51.9, -3) * mm, "end": v(52.1, -3) * mm});
            skLineSegment(sketch, "E6.10.0.31", {"start": v(50.9, -3) * mm, "end": v(51.1, -3) * mm});
            skLineSegment(sketch, "E6.10.0.32", {"start": v(53.9, -3) * mm, "end": v(54.1, -3) * mm});
            skLineSegment(sketch, "E6.10.0.33", {"start": v(57.9, -3) * mm, "end": v(58.1, -3) * mm});
            skLineSegment(sketch, "E6.10.0.34", {"start": v(58.9, -3) * mm, "end": v(59.1, -3) * mm});
            skLineSegment(sketch, "E6.10.0.35", {"start": v(58.9, -5) * mm, "end": v(59.1, -5) * mm});
            skLineSegment(sketch, "E6.10.0.36", {"start": v(57.9, -5) * mm, "end": v(58.1, -5) * mm});
            skLineSegment(sketch, "E6.10.0.37", {"start": v(54.9, -5) * mm, "end": v(55.1, -5) * mm});
            skLineSegment(sketch, "E6.10.0.38", {"start": v(53.9, -5) * mm, "end": v(54.1, -5) * mm});
            skLineSegment(sketch, "E6.10.0.39", {"start": v(55.9, -5) * mm, "end": v(56.1, -5) * mm});
            skLineSegment(sketch, "E6.10.0.40", {"start": v(55.9, -3) * mm, "end": v(56.1, -3) * mm});
            skLineSegment(sketch, "E6.10.0.41", {"start": v(50.1, -5) * mm, "end": v(49.9, -5) * mm});
            skLineSegment(sketch, "E6.10.0.42", {"start": v(52.9, -5) * mm, "end": v(53.1, -5) * mm});
            skLineSegment(sketch, "E6.10.0.43", {"start": v(52.9, -3) * mm, "end": v(53.1, -3) * mm});
            skLineSegment(sketch, "E6.10.0.44", {"start": v(56.9, -5) * mm, "end": v(57.1, -5) * mm});
            skLineSegment(sketch, "E6.10.0.45", {"start": v(56.9, -3) * mm, "end": v(57.1, -3) * mm});
            skCircle(sketch, "E6.10.0.46", {"center": v(55, -3) * mm, "radius": 0.25 * mm});
            skLineSegment(sketch, "E6.10.0.47", {"start": v(50.9, -5) * mm, "end": v(51.9, -5) * mm, "construction": true});
            skLineSegment(sketch, "E6.10.0.48", {"start": v(51.9, -5) * mm, "end": v(52.1, -5) * mm});
            skLineSegment(sketch, "E6.10.0.49", {"start": v(50.9, -5) * mm, "end": v(51.1, -5) * mm});
            skLineSegment(sketch, "E6.10.0.50", {"start": v(54.9, -3) * mm, "end": v(55.1, -3) * mm});
            skArc(sketch, "E6.10.0.51", {"start": v(50.1, -0.1) * mm, "mid": v(50, 0) * mm, "end": v(49.9, -0.1) * mm});
            skLineSegment(sketch, "E6.10.0.52", {"start": v(50.1, -0.1) * mm, "end": v(49.9, -0.1) * mm});
            skLineSegment(sketch, "E6.direction1", {"start": v(-50.1, -5) * mm, "end": v(-40.1, -5) * mm, "construction": true});
            skSolve(sketch);
        }
        {
            var Q0;
            {var subQ132=sQuery(id+"F2.wireOp",EDGE,"E1.left");Q0=makeQuery(id+"F2.imprint","IMPRINT",FACE,{"disambiguationData":[TD([[makeQuery(id+"F2.imprint","IMPRINT",EDGE,{"derivedFrom":subQ132}),-1.0]])]});}
            extrude(context, id + "F3", {"entities" : qUnion([Q0]), "operationType" : NewBodyOperationType.ADD, "depth" : .5 * mm});
        }
        {
            var Q0;
            Q0=makeQuery(id+"F1.opExtrude","CAP_FACE",FACE,{"disambiguationData":[OSD([sQuery(id+"F0.wireOp",EDGE,"E0.bottom"),sQuery(id+"F0.wireOp",EDGE,"E0.top"),sQuery(id+"F0.wireOp",EDGE,"E0.left"),sQuery(id+"F0.wireOp",EDGE,"E0.right")])],"isStart":true});
            var sketch = newSketch(context, id + "F4", { "sketchPlane" : qUnion([Q0])});
            skCircle(sketch, "E7", {"center": v(45, 0) * mm, "radius": 5 * mm});
            skSolve(sketch);
        }
        {
            var Q0;
            {var subQ0=sQuery(id+"F4.wireOp",EDGE,"E7");var subQ1=makeQuery(id+"F4.imprint","INTERSECT",VERTEX,{"derivedFrom":[makeQuery(id+"F1.opExtrude","CAP_EDGE",EDGE,{"disambiguationData":[OSD([sQuery(id+"F0.wireOp",EDGE,"E0.bottom")])],"isStart":true}),subQ0]});Q0=makeQuery(id+"F4.imprint","IMPRINT",FACE,{"disambiguationData":[TD([[makeQuery(id+"F4.imprint","IMPRINT",EDGE,{"disambiguationData":[TD([[subQ1,1.0]])],"derivedFrom":subQ0}),1.0]])]});}
            extrude(context, id + "F5", {"entities" : qUnion([Q0]), "operationType" : NewBodyOperationType.ADD, "oppositeDirection" : true, "depth" : 10 * mm});
        }
        {
            var Q0;
            {var subQ0=sQuery(id+"F2.wireOp",EDGE,"E6.6.0.24");var subQ2=sQuery(id+"F2.wireOp",EDGE,"E6.2.0.28");var subQ3=sQuery(id+"F0.wireOp",EDGE,"E0.bottom");var subQ6=sQuery(id+"F2.wireOp",EDGE,"E6.3.0.3");var subQ7=sQuery(id+"F2.wireOp",EDGE,"E6.6.0.23");var subQ9=sQuery(id+"F2.wireOp",EDGE,"E6.2.0.24");var subQ11=sQuery(id+"F2.wireOp",EDGE,"E6.2.0.29");var subQ12=sQuery(id+"F2.wireOp",EDGE,"E6.6.0.22");var subQ13=sQuery(id+"F2.wireOp",EDGE,"E6.6.0.21");var subQ14=sQuery(id+"F2.wireOp",EDGE,"E6.6.0.20");var subQ15=sQuery(id+"F2.wireOp",EDGE,"E6.7.0.13");var subQ16=sQuery(id+"F2.wireOp",EDGE,"E6.6.0.19");var subQ17=sQuery(id+"F2.wireOp",EDGE,"E6.7.0.12");var subQ18=sQuery(id+"F2.wireOp",EDGE,"E6.6.0.18");var subQ19=sQuery(id+"F2.wireOp",EDGE,"E6.7.0.11");var subQ20=sQuery(id+"F2.wireOp",EDGE,"E6.8.0.43");var subQ21=sQuery(id+"F2.wireOp",EDGE,"E6.5.0.51");var subQ22=sQuery(id+"F2.wireOp",EDGE,"E6.3.0.21");var subQ24=sQuery(id+"F2.wireOp",EDGE,"E6.1.0.15");var subQ26=sQuery(id+"F2.wireOp",EDGE,"E6.1.0.23");var subQ27=sQuery(id+"F2.wireOp",EDGE,"E6.5.0.46");var subQ28=sQuery(id+"F2.wireOp",EDGE,"E6.1.0.14");var subQ30=sQuery(id+"F2.wireOp",EDGE,"E6.1.0.16");var subQ31=sQuery(id+"F2.wireOp",EDGE,"E6.5.0.45");var subQ32=sQuery(id+"F2.wireOp",EDGE,"E6.5.0.43");var subQ33=sQuery(id+"F2.wireOp",EDGE,"E6.5.0.31");var subQ35=sQuery(id+"F2.wireOp",EDGE,"E6.5.0.13");var subQ37=sQuery(id+"F2.wireOp",EDGE,"E6.5.0.21");var subQ38=sQuery(id+"F2.wireOp",EDGE,"E6.5.0.30");var subQ40=sQuery(id+"F2.wireOp",EDGE,"E6.5.0.12");var subQ42=sQuery(id+"F2.wireOp",EDGE,"E6.5.0.22");var subQ43=sQuery(id+"F2.wireOp",EDGE,"E6.5.0.24");var subQ44=sQuery(id+"F0.wireOp",EDGE,"E0.top");var subQ45=sQuery(id+"F2.wireOp",EDGE,"E6.5.0.23");var subQ47=sQuery(id+"F2.wireOp",EDGE,"E6.7.0.19");var subQ49=sQuery(id+"F2.wireOp",EDGE,"E6.7.0.25");var subQ51=sQuery(id+"F2.wireOp",EDGE,"E6.7.0.17");var subQ53=sQuery(id+"F2.wireOp",EDGE,"E6.7.0.18");var subQ54=sQuery(id+"F2.wireOp",EDGE,"E6.7.0.51");var subQ56=sQuery(id+"F2.wireOp",EDGE,"E6.7.0.15");var subQ57=sQuery(id+"F2.wireOp",EDGE,"E6.7.0.23");var subQ58=sQuery(id+"F2.wireOp",EDGE,"E6.5.0.32");var subQ59=sQuery(id+"F2.wireOp",EDGE,"E6.3.0.14");var subQ61=sQuery(id+"F2.wireOp",EDGE,"E6.5.0.14");var subQ63=sQuery(id+"F2.wireOp",EDGE,"E6.5.0.16");var subQ64=sQuery(id+"F2.wireOp",EDGE,"E6.5.0.18");var subQ65=sQuery(id+"F2.wireOp",EDGE,"E6.6.0.11");var subQ66=sQuery(id+"F2.wireOp",EDGE,"E6.7.0.43");var subQ67=sQuery(id+"F2.wireOp",EDGE,"E6.4.0.51");var subQ68=sQuery(id+"F2.wireOp",EDGE,"E6.2.0.21");var subQ69=sQuery(id+"F2.wireOp",EDGE,"E6.5.0.40");var subQ70=sQuery(id+"F2.wireOp",EDGE,"E6.3.0.17");var subQ71=sQuery(id+"F2.wireOp",EDGE,"E6.4.0.46");var subQ72=sQuery(id+"F2.wireOp",EDGE,"E6.4.0.45");var subQ73=sQuery(id+"F2.wireOp",EDGE,"E6.4.0.43");var subQ74=sQuery(id+"F2.wireOp",EDGE,"E6.4.0.32");var subQ75=sQuery(id+"F2.wireOp",EDGE,"E6.8.0.18");var subQ77=sQuery(id+"F2.wireOp",EDGE,"E6.2.0.14");var subQ79=sQuery(id+"F2.wireOp",EDGE,"E6.2.0.16");var subQ80=sQuery(id+"F2.wireOp",EDGE,"E6.5.0.28");var subQ81=sQuery(id+"F2.wireOp",EDGE,"E6.4.0.31");var subQ83=sQuery(id+"F2.wireOp",EDGE,"E6.2.0.13");var subQ84=sQuery(id+"F2.wireOp",EDGE,"E6.5.0.27");var subQ85=sQuery(id+"F2.wireOp",EDGE,"E6.4.0.30");var subQ87=sQuery(id+"F2.wireOp",EDGE,"E6.2.0.12");var subQ89=sQuery(id+"F2.wireOp",EDGE,"E6.2.0.22");var subQ90=sQuery(id+"F2.wireOp",EDGE,"E6.5.0.26");var subQ91=sQuery(id+"F2.wireOp",EDGE,"E6.4.0.29");var subQ92=sQuery(id+"F2.wireOp",EDGE,"E6.2.0.11");var subQ93=sQuery(id+"F2.wireOp",EDGE,"E6.2.0.26");var subQ94=sQuery(id+"F2.wireOp",EDGE,"E6.4.0.28");var subQ95=sQuery(id+"F2.wireOp",EDGE,"E6.2.0.3");var subQ96=sQuery(id+"F2.wireOp",EDGE,"E6.4.0.25");var subQ97=sQuery(id+"F2.wireOp",EDGE,"E6.4.0.24");var subQ98=sQuery(id+"F2.wireOp",EDGE,"E6.5.0.20");var subQ99=sQuery(id+"F2.wireOp",EDGE,"E6.4.0.23");var subQ101=sQuery(id+"F2.wireOp",EDGE,"E6.4.0.19");var subQ103=sQuery(id+"F2.wireOp",EDGE,"E6.5.0.19");var subQ104=sQuery(id+"F2.wireOp",EDGE,"E6.4.0.22");var subQ106=sQuery(id+"F2.wireOp",EDGE,"E6.4.0.17");var subQ108=sQuery(id+"F2.wireOp",EDGE,"E6.4.0.18");var subQ109=sQuery(id+"F2.wireOp",EDGE,"E6.4.0.21");var subQ110=sQuery(id+"F2.wireOp",EDGE,"E6.6.0.51");var subQ112=sQuery(id+"F2.wireOp",EDGE,"E6.4.0.15");var subQ113=sQuery(id+"F2.wireOp",EDGE,"E4.6.0.3");var subQ114=sQuery(id+"F2.wireOp",EDGE,"E6.4.0.3");var subQ115=sQuery(id+"F2.wireOp",EDGE,"E6.6.0.28");var subQ116=sQuery(id+"F2.wireOp",EDGE,"E6.3.0.51");var subQ117=sQuery(id+"F2.wireOp",EDGE,"E6.1.0.21");var subQ118=sQuery(id+"F2.wireOp",EDGE,"E6.4.0.40");var subQ119=sQuery(id+"F2.wireOp",EDGE,"E6.2.0.17");var subQ120=sQuery(id+"F2.wireOp",EDGE,"E6.3.0.46");var subQ121=sQuery(id+"F2.wireOp",EDGE,"E6.4.0.34");var subQ122=sQuery(id+"F2.wireOp",EDGE,"E6.3.0.45");var subQ123=sQuery(id+"F2.wireOp",EDGE,"E6.4.0.33");var subQ124=sQuery(id+"F2.wireOp",EDGE,"E6.3.0.43");var subQ125=sQuery(id+"F2.wireOp",EDGE,"E6.4.0.27");var subQ126=sQuery(id+"F2.wireOp",EDGE,"E6.3.0.30");var subQ127=sQuery(id+"F2.wireOp",EDGE,"E6.4.0.26");var subQ128=sQuery(id+"F2.wireOp",EDGE,"E6.3.0.29");var subQ129=sQuery(id+"F2.wireOp",EDGE,"E6.3.0.28");var subQ130=sQuery(id+"F2.wireOp",EDGE,"E6.1.0.3");var subQ131=sQuery(id+"F2.wireOp",EDGE,"E6.3.0.27");var subQ132=sQuery(id+"F2.wireOp",EDGE,"E6.3.0.26");var subQ133=sQuery(id+"F2.wireOp",EDGE,"E6.3.0.25");var subQ134=sQuery(id+"F2.wireOp",EDGE,"E6.3.0.24");var subQ135=sQuery(id+"F2.wireOp",EDGE,"E6.4.0.20");var subQ136=sQuery(id+"F2.wireOp",EDGE,"E6.3.0.23");var subQ137=sQuery(id+"F2.wireOp",EDGE,"E6.3.0.22");var subQ138=sQuery(id+"F2.wireOp",EDGE,"E6.1.0.17");var subQ140=sQuery(id+"F2.wireOp",EDGE,"E6.1.0.18");var subQ141=sQuery(id+"F2.wireOp",EDGE,"E6.3.0.31");var subQ142=sQuery(id+"F2.wireOp",EDGE,"E6.1.0.13");var subQ143=sQuery(id+"F2.wireOp",EDGE,"E6.2.0.46");var subQ144=sQuery(id+"F2.wireOp",EDGE,"E6.3.0.16");var subQ145=sQuery(id+"F2.wireOp",EDGE,"E6.2.0.23");var subQ146=sQuery(id+"F2.wireOp",EDGE,"E6.3.0.15");var subQ147=sQuery(id+"F2.wireOp",EDGE,"E6.3.0.13");var subQ148=sQuery(id+"F2.wireOp",EDGE,"E6.2.0.18");var subQ149=sQuery(id+"F2.wireOp",EDGE,"E4.5.0.0");var subQ150=sQuery(id+"F2.wireOp",EDGE,"E4.2.0.4");var subQ151=sQuery(id+"F2.wireOp",EDGE,"E6.2.0.51");var subQ152=sQuery(id+"F2.wireOp",EDGE,"E6.4.0.11");var subQ153=sQuery(id+"F2.wireOp",EDGE,"E4.6.0.4");var subQ154=sQuery(id+"F2.wireOp",EDGE,"E6.1.0.29");var subQ155=sQuery(id+"F2.wireOp",EDGE,"E4.8.0.0");var subQ156=sQuery(id+"F2.wireOp",EDGE,"E4.3.0.0");var subQ157=sQuery(id+"F2.wireOp",EDGE,"E6.5.0.11");var subQ158=sQuery(id+"F2.wireOp",EDGE,"E6.6.0.43");var subQ159=sQuery(id+"F2.wireOp",EDGE,"E6.4.0.14");var subQ160=sQuery(id+"F2.wireOp",EDGE,"E6.6.0.32");var subQ161=sQuery(id+"F2.wireOp",EDGE,"E4.4.0.3");var subQ163=sQuery(id+"F2.wireOp",EDGE,"E4.5.0.4");var subQ166=sQuery(id+"F2.wireOp",EDGE,"E6.8.0.14");var subQ168=sQuery(id+"F2.wireOp",EDGE,"E6.8.0.16");var subQ169=sQuery(id+"F2.wireOp",EDGE,"E6.1.0.32");var subQ170=sQuery(id+"F2.wireOp",EDGE,"E6.5.0.25");var subQ171=sQuery(id+"F2.wireOp",EDGE,"E4.7.0.4");var subQ172=sQuery(id+"F2.wireOp",EDGE,"E6.3.0.18");var subQ173=sQuery(id+"F2.wireOp",EDGE,"E6.4.0.13");var subQ174=sQuery(id+"F2.wireOp",EDGE,"E4.7.0.3");var subQ175=sQuery(id+"F2.wireOp",EDGE,"E6.1.0.27");var subQ176=sQuery(id+"F2.wireOp",EDGE,"E4.6.0.0");var subQ177=sQuery(id+"F2.wireOp",EDGE,"E1.left");var subQ178=sQuery(id+"F2.wireOp",EDGE,"E6.1.0.34");var subQ179=sQuery(id+"F2.wireOp",EDGE,"E4.3.0.3");var subQ180=sQuery(id+"F2.wireOp",EDGE,"E6.4.0.16");var subQ183=sQuery(id+"F2.wireOp",EDGE,"E4.8.0.3");var subQ184=sQuery(id+"F2.wireOp",EDGE,"E6.1.0.30");var subQ185=sQuery(id+"F2.wireOp",EDGE,"E4.5.0.3");var subQ186=sQuery(id+"F2.wireOp",EDGE,"E6.1.0.33");var subQ187=sQuery(id+"F2.wireOp",EDGE,"E6.4.0.12");var subQ188=sQuery(id+"F2.wireOp",EDGE,"E4.7.0.0");var subQ189=sQuery(id+"F2.wireOp",EDGE,"E4.1.0.0");var subQ190=sQuery(id+"F2.wireOp",EDGE,"E3.right");var subQ191=sQuery(id+"F2.wireOp",EDGE,"E6.1.0.12");var subQ192=sQuery(id+"F2.wireOp",EDGE,"E4.2.0.0");var subQ193=sQuery(id+"F2.wireOp",EDGE,"E6.1.0.19");var subQ194=sQuery(id+"F2.wireOp",EDGE,"E6.6.0.3");var subQ195=sQuery(id+"F2.wireOp",EDGE,"E6.7.0.40");var subQ196=sQuery(id+"F2.wireOp",EDGE,"E6.8.0.28");var subQ197=sQuery(id+"F2.wireOp",EDGE,"E6.1.0.20");var subQ198=sQuery(id+"F2.wireOp",EDGE,"E6.1.0.51");var subQ199=sQuery(id+"F2.wireOp",EDGE,"E3.left");var subQ200=sQuery(id+"F2.wireOp",EDGE,"E6.5.0.29");var subQ202=sQuery(id+"F2.wireOp",EDGE,"E5");var subQ203=sQuery(id+"F2.wireOp",EDGE,"E4.8.0.4");var subQ204=sQuery(id+"F2.wireOp",EDGE,"E6.1.0.31");var subQ205=sQuery(id+"F2.wireOp",EDGE,"E6.1.0.40");var subQ206=sQuery(id+"F2.wireOp",EDGE,"E6.5.0.33");var subQ207=sQuery(id+"F2.wireOp",EDGE,"E6.6.0.26");var subQ208=sQuery(id+"F2.wireOp",EDGE,"E6.10.0.3");var subQ209=sQuery(id+"F2.wireOp",EDGE,"E6.9.0.51");var subQ210=sQuery(id+"F2.wireOp",EDGE,"E6.9.0.29");var subQ211=sQuery(id+"F2.wireOp",EDGE,"E6.9.0.28");var subQ212=sQuery(id+"F2.wireOp",EDGE,"E6.9.0.27");var subQ213=sQuery(id+"F2.wireOp",EDGE,"E6.9.0.26");var subQ214=sQuery(id+"F2.wireOp",EDGE,"E6.9.0.25");var subQ215=sQuery(id+"F2.wireOp",EDGE,"E6.9.0.24");var subQ216=sQuery(id+"F2.wireOp",EDGE,"E6.9.0.23");var subQ217=sQuery(id+"F2.wireOp",EDGE,"E6.9.0.22");var subQ218=sQuery(id+"F2.wireOp",EDGE,"E6.9.0.21");var subQ219=sQuery(id+"F2.wireOp",EDGE,"E6.9.0.20");var subQ220=sQuery(id+"F2.wireOp",EDGE,"E6.9.0.19");var subQ221=sQuery(id+"F2.wireOp",EDGE,"E6.9.0.18");var subQ222=sQuery(id+"F2.wireOp",EDGE,"E6.9.0.17");var subQ223=sQuery(id+"F2.wireOp",EDGE,"E6.9.0.16");var subQ224=sQuery(id+"F2.wireOp",EDGE,"E6.9.0.15");var subQ225=sQuery(id+"F2.wireOp",EDGE,"E6.9.0.14");var subQ226=sQuery(id+"F2.wireOp",EDGE,"E6.9.0.13");var subQ227=sQuery(id+"F2.wireOp",EDGE,"E6.9.0.12");var subQ228=sQuery(id+"F2.wireOp",EDGE,"E6.9.0.11");var subQ229=sQuery(id+"F2.wireOp",EDGE,"E6.9.0.3");var subQ230=sQuery(id+"F2.wireOp",EDGE,"E6.8.0.51");var subQ231=sQuery(id+"F2.wireOp",EDGE,"E6.8.0.46");var subQ232=sQuery(id+"F2.wireOp",EDGE,"E6.8.0.45");var subQ233=sQuery(id+"F2.wireOp",EDGE,"E6.8.0.40");var subQ234=sQuery(id+"F2.wireOp",EDGE,"E6.8.0.34");var subQ235=sQuery(id+"F2.wireOp",EDGE,"E6.8.0.33");var subQ236=sQuery(id+"F2.wireOp",EDGE,"E6.8.0.32");var subQ237=sQuery(id+"F2.wireOp",EDGE,"E6.8.0.31");var subQ238=sQuery(id+"F2.wireOp",EDGE,"E6.8.0.30");var subQ239=sQuery(id+"F2.wireOp",EDGE,"E6.8.0.29");var subQ240=sQuery(id+"F2.wireOp",EDGE,"E6.8.0.27");var subQ241=sQuery(id+"F2.wireOp",EDGE,"E6.8.0.26");var subQ242=sQuery(id+"F2.wireOp",EDGE,"E6.8.0.25");var subQ243=sQuery(id+"F2.wireOp",EDGE,"E6.8.0.24");var subQ244=sQuery(id+"F2.wireOp",EDGE,"E6.8.0.23");var subQ245=sQuery(id+"F2.wireOp",EDGE,"E6.8.0.22");var subQ246=sQuery(id+"F2.wireOp",EDGE,"E6.8.0.21");var subQ247=sQuery(id+"F2.wireOp",EDGE,"E6.8.0.20");var subQ248=sQuery(id+"F2.wireOp",EDGE,"E6.8.0.19");var subQ249=sQuery(id+"F2.wireOp",EDGE,"E6.8.0.17");var subQ250=sQuery(id+"F2.wireOp",EDGE,"E6.8.0.15");var subQ251=sQuery(id+"F2.wireOp",EDGE,"E6.8.0.13");var subQ252=sQuery(id+"F2.wireOp",EDGE,"E6.8.0.12");var subQ253=sQuery(id+"F2.wireOp",EDGE,"E6.8.0.11");var subQ254=sQuery(id+"F2.wireOp",EDGE,"E6.8.0.3");var subQ255=sQuery(id+"F2.wireOp",EDGE,"E6.7.0.46");var subQ256=sQuery(id+"F2.wireOp",EDGE,"E6.7.0.45");var subQ257=sQuery(id+"F2.wireOp",EDGE,"E6.7.0.34");var subQ258=sQuery(id+"F2.wireOp",EDGE,"E6.7.0.33");var subQ259=sQuery(id+"F2.wireOp",EDGE,"E6.7.0.32");var subQ260=sQuery(id+"F2.wireOp",EDGE,"E6.7.0.31");var subQ261=sQuery(id+"F2.wireOp",EDGE,"E6.7.0.30");var subQ262=sQuery(id+"F2.wireOp",EDGE,"E6.7.0.29");var subQ263=sQuery(id+"F2.wireOp",EDGE,"E6.7.0.28");var subQ264=sQuery(id+"F2.wireOp",EDGE,"E6.7.0.27");var subQ265=sQuery(id+"F2.wireOp",EDGE,"E6.7.0.26");var subQ266=sQuery(id+"F2.wireOp",EDGE,"E6.7.0.24");var subQ267=sQuery(id+"F2.wireOp",EDGE,"E6.7.0.22");var subQ268=sQuery(id+"F2.wireOp",EDGE,"E6.7.0.21");var subQ269=sQuery(id+"F2.wireOp",EDGE,"E6.7.0.20");var subQ270=sQuery(id+"F2.wireOp",EDGE,"E6.7.0.16");var subQ271=sQuery(id+"F2.wireOp",EDGE,"E6.7.0.14");var subQ272=sQuery(id+"F2.wireOp",EDGE,"E6.7.0.3");var subQ273=sQuery(id+"F2.wireOp",EDGE,"E6.6.0.46");var subQ274=sQuery(id+"F2.wireOp",EDGE,"E6.6.0.45");var subQ275=sQuery(id+"F2.wireOp",EDGE,"E6.6.0.40");var subQ276=sQuery(id+"F2.wireOp",EDGE,"E6.6.0.34");var subQ277=sQuery(id+"F2.wireOp",EDGE,"E6.6.0.33");var subQ278=sQuery(id+"F2.wireOp",EDGE,"E6.6.0.31");var subQ279=sQuery(id+"F2.wireOp",EDGE,"E6.6.0.30");var subQ280=sQuery(id+"F2.wireOp",EDGE,"E6.6.0.29");var subQ281=sQuery(id+"F2.wireOp",EDGE,"E6.6.0.27");var subQ282=sQuery(id+"F2.wireOp",EDGE,"E6.6.0.25");var subQ283=sQuery(id+"F2.wireOp",EDGE,"E6.6.0.17");var subQ284=sQuery(id+"F2.wireOp",EDGE,"E6.6.0.16");var subQ285=sQuery(id+"F2.wireOp",EDGE,"E6.6.0.15");var subQ286=sQuery(id+"F2.wireOp",EDGE,"E6.6.0.14");var subQ287=sQuery(id+"F2.wireOp",EDGE,"E6.6.0.13");var subQ288=sQuery(id+"F2.wireOp",EDGE,"E6.6.0.12");var subQ289=sQuery(id+"F2.wireOp",EDGE,"E6.5.0.34");var subQ290=sQuery(id+"F2.wireOp",EDGE,"E6.5.0.17");var subQ291=sQuery(id+"F2.wireOp",EDGE,"E6.5.0.15");var subQ292=sQuery(id+"F2.wireOp",EDGE,"E6.5.0.3");var subQ293=sQuery(id+"F2.wireOp",EDGE,"E6.3.0.40");var subQ294=sQuery(id+"F2.wireOp",EDGE,"E6.3.0.34");var subQ295=sQuery(id+"F2.wireOp",EDGE,"E6.3.0.33");var subQ296=sQuery(id+"F2.wireOp",EDGE,"E6.3.0.32");var subQ297=sQuery(id+"F2.wireOp",EDGE,"E6.3.0.20");var subQ298=sQuery(id+"F2.wireOp",EDGE,"E6.3.0.19");var subQ299=sQuery(id+"F2.wireOp",EDGE,"E6.3.0.12");var subQ300=sQuery(id+"F2.wireOp",EDGE,"E6.3.0.11");var subQ301=sQuery(id+"F2.wireOp",EDGE,"E6.2.0.45");var subQ302=sQuery(id+"F2.wireOp",EDGE,"E6.2.0.43");var subQ303=sQuery(id+"F2.wireOp",EDGE,"E6.2.0.40");var subQ304=sQuery(id+"F2.wireOp",EDGE,"E6.2.0.34");var subQ305=sQuery(id+"F2.wireOp",EDGE,"E6.2.0.33");var subQ306=sQuery(id+"F2.wireOp",EDGE,"E6.2.0.32");var subQ307=sQuery(id+"F2.wireOp",EDGE,"E6.2.0.31");var subQ308=sQuery(id+"F2.wireOp",EDGE,"E6.2.0.30");var subQ309=sQuery(id+"F2.wireOp",EDGE,"E6.2.0.27");var subQ310=sQuery(id+"F2.wireOp",EDGE,"E6.2.0.25");var subQ311=sQuery(id+"F2.wireOp",EDGE,"E6.2.0.20");var subQ312=sQuery(id+"F2.wireOp",EDGE,"E6.2.0.19");var subQ313=sQuery(id+"F2.wireOp",EDGE,"E6.2.0.15");var subQ314=sQuery(id+"F2.wireOp",EDGE,"E6.1.0.46");var subQ315=sQuery(id+"F2.wireOp",EDGE,"E6.1.0.45");var subQ316=sQuery(id+"F2.wireOp",EDGE,"E6.1.0.43");var subQ317=sQuery(id+"F2.wireOp",EDGE,"E6.1.0.28");var subQ318=sQuery(id+"F2.wireOp",EDGE,"E6.1.0.26");var subQ319=sQuery(id+"F2.wireOp",EDGE,"E6.1.0.25");var subQ320=sQuery(id+"F2.wireOp",EDGE,"E6.1.0.24");var subQ321=sQuery(id+"F2.wireOp",EDGE,"E6.1.0.22");var subQ322=sQuery(id+"F2.wireOp",EDGE,"E6.1.0.11");var subQ323=sQuery(id+"F2.wireOp",EDGE,"E4.4.0.4");var subQ324=sQuery(id+"F2.wireOp",EDGE,"E4.3.0.4");var subQ325=sQuery(id+"F2.wireOp",EDGE,"E4.2.0.3");var subQ326=sQuery(id+"F2.wireOp",EDGE,"E4.1.0.4");var subQ327=sQuery(id+"F2.wireOp",EDGE,"E4.1.0.3");var subQ328=sQuery(id+"F2.wireOp",EDGE,"E3.bottom");var subQ329=sQuery(id+"F2.wireOp",EDGE,"E2");var subQ330=sQuery(id+"F0.wireOp",EDGE,"E0.right");var subQ331=makeQuery(id+"F3.opExtrude","CAP_FACE",FACE,{"disambiguationData":[OSD([subQ3,subQ44,sQuery(id+"F0.wireOp",EDGE,"E0.left"),subQ330,subQ177,subQ329,subQ328,subQ199,subQ190,subQ189,subQ327,subQ326,subQ192,subQ325,subQ150,subQ156,subQ179,subQ324,subQ161,subQ323,subQ149,subQ185,subQ163,subQ176,subQ113,subQ153,subQ188,subQ174,subQ171,subQ155,subQ183,subQ203,subQ202,subQ130,subQ322,subQ191,subQ142,subQ28,subQ24,subQ30,subQ138,subQ140,subQ193,subQ197,subQ117,subQ321,subQ26,subQ320,subQ319,subQ318,subQ175,subQ317,subQ154,subQ184,subQ204,subQ169,subQ186,subQ178,subQ205,subQ316,subQ315,subQ314,subQ198,subQ95,subQ92,subQ87,subQ83,subQ77,subQ313,subQ79,subQ119,subQ148,subQ312,subQ311,subQ68,subQ89,subQ145,subQ9,subQ310,subQ93,subQ309,subQ2,subQ11,subQ308,subQ307,subQ306,subQ305,subQ304,subQ303,subQ302,subQ301,subQ143,subQ151,subQ6,subQ300,subQ299,subQ147,subQ59,subQ146,subQ144,subQ70,subQ172,subQ298,subQ297,subQ22,subQ137,subQ136,subQ134,subQ133,subQ132,subQ131,subQ129,subQ128,subQ126,subQ141,subQ296,subQ295,subQ294,subQ293,subQ124,subQ122,subQ120,subQ116,subQ114,subQ152,subQ187,subQ173,subQ159,subQ112,subQ180,subQ106,subQ108,subQ101,subQ135,subQ109,subQ104,subQ99,subQ97,subQ96,subQ127,subQ125,subQ94,subQ91,subQ85,subQ81,subQ74,subQ123,subQ121,subQ118,subQ73,subQ72,subQ71,subQ67,subQ292,subQ157,subQ40,subQ35,subQ61,subQ291,subQ63,subQ290,subQ64,subQ103,subQ98,subQ37,subQ42,subQ45,subQ43,subQ170,subQ90,subQ84,subQ80,subQ200,subQ38,subQ33,subQ58,subQ206,subQ289,subQ69,subQ32,subQ31,subQ27,subQ21,subQ194,subQ65,subQ288,subQ287,subQ286,subQ285,subQ284,subQ283,subQ18,subQ16,subQ14,subQ13,subQ12,subQ7,subQ0,subQ282,subQ207,subQ281,subQ115,subQ280,subQ279,subQ278,subQ160,subQ277,subQ276,subQ275,subQ158,subQ274,subQ273,subQ110,subQ272,subQ19,subQ17,subQ15,subQ271,subQ56,subQ270,subQ51,subQ53,subQ47,subQ269,subQ268,subQ267,subQ57,subQ266,subQ49,subQ265,subQ264,subQ263,subQ262,subQ261,subQ260,subQ259,subQ258,subQ257,subQ195,subQ66,subQ256,subQ255,subQ54,subQ254,subQ253,subQ252,subQ251,subQ166,subQ250,subQ168,subQ249,subQ75,subQ248,subQ247,subQ246,subQ245,subQ244,subQ243,subQ242,subQ241,subQ240,subQ196,subQ239,subQ238,subQ237,subQ236,subQ235,subQ234,subQ233,subQ20,subQ232,subQ231,subQ230,subQ229,subQ228,subQ227,subQ226,subQ225,subQ224,subQ223,subQ222,subQ221,subQ220,subQ219,subQ218,subQ217,subQ216,subQ215,subQ214,subQ213,subQ212,subQ211,subQ210,sQuery(id+"F2.wireOp",EDGE,"E6.9.0.30"),sQuery(id+"F2.wireOp",EDGE,"E6.9.0.31"),sQuery(id+"F2.wireOp",EDGE,"E6.9.0.32"),sQuery(id+"F2.wireOp",EDGE,"E6.9.0.33"),sQuery(id+"F2.wireOp",EDGE,"E6.9.0.34"),sQuery(id+"F2.wireOp",EDGE,"E6.9.0.40"),sQuery(id+"F2.wireOp",EDGE,"E6.9.0.43"),sQuery(id+"F2.wireOp",EDGE,"E6.9.0.45"),sQuery(id+"F2.wireOp",EDGE,"E6.9.0.46"),subQ209,subQ208,sQuery(id+"F2.wireOp",EDGE,"E6.10.0.51")])],"isStart":false});Q0=makeQuery(id+"F5.boolean.opBoolean","SPLIT",FACE,{"disambiguationData":[TD([makeQuery(id+"F1.opExtrude","SWEPT_FACE",FACE,{"disambiguationData":[OSD([subQ330])]})])],"derivedFrom":subQ331});}
            var sketch = newSketch(context, id + "F6", { "sketchPlane" : qUnion([Q0])});
            skText(sketch, "E8", { "text": "10 mm x 100 mm, 1 mm thick + 10mm cylinder", "fontName": "OpenSans-Bold.ttf"});
            const initialGuessF6  = {"E8": [-0.03805, 0.00121, 1, 0, 0.00236]};
            skSetInitialGuess(sketch, initialGuessF6);
            skSolve(sketch);
        }
        {
            var Q0;
            Q0=makeQuery(id+"F6.imprint","IMPRINT",FACE,{"disambiguationData":[TD([[makeQuery(id+"F6.imprint","IMPRINT",EDGE,{"derivedFrom":sQuery(id+"F6.wireOp",EDGE,"E8.sketch_text.stroke-0")}),-1.0]])]});
            var Q1;
            Q1=makeQuery(id+"F6.imprint","IMPRINT",FACE,{"disambiguationData":[TD([[makeQuery(id+"F6.imprint","IMPRINT",EDGE,{"derivedFrom":sQuery(id+"F6.wireOp",EDGE,"E8.sketch_text.stroke-10")}),-1.0]])]});
            var Q2;
            Q2=makeQuery(id+"F6.imprint","IMPRINT",FACE,{"disambiguationData":[TD([[makeQuery(id+"F6.imprint","IMPRINT",EDGE,{"derivedFrom":sQuery(id+"F6.wireOp",EDGE,"E8.sketch_text.stroke-26")}),-1.0]])]});
            var Q3;
            Q3=makeQuery(id+"F6.imprint","IMPRINT",FACE,{"disambiguationData":[TD([[makeQuery(id+"F6.imprint","IMPRINT",EDGE,{"derivedFrom":sQuery(id+"F6.wireOp",EDGE,"E8.sketch_text.stroke-54")}),-1.0]])]});
            var Q4;
            Q4=makeQuery(id+"F6.imprint","IMPRINT",FACE,{"disambiguationData":[TD([[makeQuery(id+"F6.imprint","IMPRINT",EDGE,{"derivedFrom":sQuery(id+"F6.wireOp",EDGE,"E8.sketch_text.stroke-82")}),-1.0]])]});
            var Q5;
            Q5=makeQuery(id+"F6.imprint","IMPRINT",FACE,{"disambiguationData":[TD([[makeQuery(id+"F6.imprint","IMPRINT",EDGE,{"derivedFrom":sQuery(id+"F6.wireOp",EDGE,"E8.sketch_text.stroke-94")}),-1.0]])]});
            var Q6;
            Q6=makeQuery(id+"F6.imprint","IMPRINT",FACE,{"disambiguationData":[TD([[makeQuery(id+"F6.imprint","IMPRINT",EDGE,{"derivedFrom":sQuery(id+"F6.wireOp",EDGE,"E8.sketch_text.stroke-104")}),-1.0]])]});
            var Q7;
            Q7=makeQuery(id+"F6.imprint","IMPRINT",FACE,{"disambiguationData":[TD([[makeQuery(id+"F6.imprint","IMPRINT",EDGE,{"derivedFrom":sQuery(id+"F6.wireOp",EDGE,"E8.sketch_text.stroke-120")}),-1.0]])]});
            var Q8;
            Q8=makeQuery(id+"F6.imprint","IMPRINT",FACE,{"disambiguationData":[TD([[makeQuery(id+"F6.imprint","IMPRINT",EDGE,{"derivedFrom":sQuery(id+"F6.wireOp",EDGE,"E8.sketch_text.stroke-136")}),-1.0]])]});
            var Q9;
            Q9=makeQuery(id+"F6.imprint","IMPRINT",FACE,{"disambiguationData":[TD([[makeQuery(id+"F6.imprint","IMPRINT",EDGE,{"derivedFrom":sQuery(id+"F6.wireOp",EDGE,"E8.sketch_text.stroke-164")}),-1.0]])]});
            var Q10;
            Q10=makeQuery(id+"F6.imprint","IMPRINT",FACE,{"disambiguationData":[TD([[makeQuery(id+"F6.imprint","IMPRINT",EDGE,{"derivedFrom":sQuery(id+"F6.wireOp",EDGE,"E8.sketch_text.stroke-192")}),-1.0]])]});
            var Q11;
            Q11=makeQuery(id+"F6.imprint","IMPRINT",FACE,{"disambiguationData":[TD([[makeQuery(id+"F6.imprint","IMPRINT",EDGE,{"derivedFrom":sQuery(id+"F6.wireOp",EDGE,"E8.sketch_text.stroke-197")}),-1.0]])]});
            var Q12;
            Q12=makeQuery(id+"F6.imprint","IMPRINT",FACE,{"disambiguationData":[TD([[makeQuery(id+"F6.imprint","IMPRINT",EDGE,{"derivedFrom":sQuery(id+"F6.wireOp",EDGE,"E8.sketch_text.stroke-207")}),-1.0]])]});
            var Q13;
            Q13=makeQuery(id+"F6.imprint","IMPRINT",FACE,{"disambiguationData":[TD([[makeQuery(id+"F6.imprint","IMPRINT",EDGE,{"derivedFrom":sQuery(id+"F6.wireOp",EDGE,"E8.sketch_text.stroke-235")}),-1.0]])]});
            var Q14;
            Q14=makeQuery(id+"F6.imprint","IMPRINT",FACE,{"disambiguationData":[TD([[makeQuery(id+"F6.imprint","IMPRINT",EDGE,{"derivedFrom":sQuery(id+"F6.wireOp",EDGE,"E8.sketch_text.stroke-263")}),-1.0]])]});
            var Q15;
            Q15=makeQuery(id+"F6.imprint","IMPRINT",FACE,{"disambiguationData":[TD([[makeQuery(id+"F6.imprint","IMPRINT",EDGE,{"derivedFrom":sQuery(id+"F6.wireOp",EDGE,"E8.sketch_text.stroke-281")}),-1.0]])]});
            var Q16;
            Q16=makeQuery(id+"F6.imprint","IMPRINT",FACE,{"disambiguationData":[TD([[makeQuery(id+"F6.imprint","IMPRINT",EDGE,{"derivedFrom":sQuery(id+"F6.wireOp",EDGE,"E8.sketch_text.stroke-303")}),-1.0]])]});
            var Q17;
            Q17=makeQuery(id+"F6.imprint","IMPRINT",FACE,{"disambiguationData":[TD([[makeQuery(id+"F6.imprint","IMPRINT",EDGE,{"derivedFrom":sQuery(id+"F6.wireOp",EDGE,"E8.sketch_text.stroke-298")}),-1.0]])]});
            var Q18;
            Q18=makeQuery(id+"F6.imprint","IMPRINT",FACE,{"disambiguationData":[TD([[makeQuery(id+"F6.imprint","IMPRINT",EDGE,{"derivedFrom":sQuery(id+"F6.wireOp",EDGE,"E8.sketch_text.stroke-307")}),-1.0]])]});
            var Q19;
            Q19=makeQuery(id+"F6.imprint","IMPRINT",FACE,{"disambiguationData":[TD([[makeQuery(id+"F6.imprint","IMPRINT",EDGE,{"derivedFrom":sQuery(id+"F6.wireOp",EDGE,"E8.sketch_text.stroke-321")}),-1.0]])]});
            var Q20;
            Q20=makeQuery(id+"F6.imprint","IMPRINT",FACE,{"disambiguationData":[TD([[makeQuery(id+"F6.imprint","IMPRINT",EDGE,{"derivedFrom":sQuery(id+"F6.wireOp",EDGE,"E8.sketch_text.stroke-336")}),-1.0]])]});
            var Q21;
            Q21=makeQuery(id+"F6.imprint","IMPRINT",FACE,{"disambiguationData":[TD([[makeQuery(id+"F6.imprint","IMPRINT",EDGE,{"derivedFrom":sQuery(id+"F6.wireOp",EDGE,"E8.sketch_text.stroke-348")}),-1.0]])]});
            var Q22;
            Q22=makeQuery(id+"F6.imprint","IMPRINT",FACE,{"disambiguationData":[TD([[makeQuery(id+"F6.imprint","IMPRINT",EDGE,{"derivedFrom":sQuery(id+"F6.wireOp",EDGE,"E8.sketch_text.stroke-358")}),-1.0]])]});
            var Q23;
            Q23=makeQuery(id+"F6.imprint","IMPRINT",FACE,{"disambiguationData":[TD([[makeQuery(id+"F6.imprint","IMPRINT",EDGE,{"derivedFrom":sQuery(id+"F6.wireOp",EDGE,"E8.sketch_text.stroke-374")}),-1.0]])]});
            var Q24;
            Q24=makeQuery(id+"F6.imprint","IMPRINT",FACE,{"disambiguationData":[TD([[makeQuery(id+"F6.imprint","IMPRINT",EDGE,{"derivedFrom":sQuery(id+"F6.wireOp",EDGE,"E8.sketch_text.stroke-402")}),-1.0]])]});
            var Q25;
            Q25=makeQuery(id+"F6.imprint","IMPRINT",FACE,{"disambiguationData":[TD([[makeQuery(id+"F6.imprint","IMPRINT",EDGE,{"derivedFrom":sQuery(id+"F6.wireOp",EDGE,"E8.sketch_text.stroke-430")}),-1.0]])]});
            var Q26;
            Q26=makeQuery(id+"F6.imprint","IMPRINT",FACE,{"disambiguationData":[TD([[makeQuery(id+"F6.imprint","IMPRINT",EDGE,{"derivedFrom":sQuery(id+"F6.wireOp",EDGE,"E8.sketch_text.stroke-444")}),-1.0]])]});
            var Q27;
            Q27=makeQuery(id+"F6.imprint","IMPRINT",FACE,{"disambiguationData":[TD([[makeQuery(id+"F6.imprint","IMPRINT",EDGE,{"derivedFrom":sQuery(id+"F6.wireOp",EDGE,"E8.sketch_text.stroke-461")}),-1.0]])]});
            var Q28;
            Q28=makeQuery(id+"F6.imprint","IMPRINT",FACE,{"disambiguationData":[TD([[makeQuery(id+"F6.imprint","IMPRINT",EDGE,{"derivedFrom":sQuery(id+"F6.wireOp",EDGE,"E8.sketch_text.stroke-470")}),-1.0]])]});
            var Q29;
            Q29=makeQuery(id+"F6.imprint","IMPRINT",FACE,{"disambiguationData":[TD([[makeQuery(id+"F6.imprint","IMPRINT",EDGE,{"derivedFrom":sQuery(id+"F6.wireOp",EDGE,"E8.sketch_text.stroke-474")}),-1.0]])]});
            var Q30;
            Q30=makeQuery(id+"F6.imprint","IMPRINT",FACE,{"disambiguationData":[TD([[makeQuery(id+"F6.imprint","IMPRINT",EDGE,{"derivedFrom":sQuery(id+"F6.wireOp",EDGE,"E8.sketch_text.stroke-465")}),-1.0]])]});
            var Q31;
            Q31=makeQuery(id+"F6.imprint","IMPRINT",FACE,{"disambiguationData":[TD([[makeQuery(id+"F6.imprint","IMPRINT",EDGE,{"derivedFrom":sQuery(id+"F6.wireOp",EDGE,"E8.sketch_text.stroke-491")}),-1.0]])]});
            var Q32;
            Q32=makeQuery(id+"F6.imprint","IMPRINT",FACE,{"disambiguationData":[TD([[makeQuery(id+"F6.imprint","IMPRINT",EDGE,{"derivedFrom":sQuery(id+"F6.wireOp",EDGE,"E8.sketch_text.stroke-514")}),-1.0]])]});
            var Q33;
            Q33=makeQuery(id+"F6.imprint","IMPRINT",FACE,{"disambiguationData":[TD([[makeQuery(id+"F6.imprint","IMPRINT",EDGE,{"derivedFrom":sQuery(id+"F6.wireOp",EDGE,"E8.sketch_text.stroke-534")}),-1.0]])]});
            extrude(context, id + "F7", {"entities" : qUnion([Q0, Q1, Q2, Q3, Q4, Q5, Q6, Q7, Q8, Q9, Q10, Q11, Q12, Q13, Q14, Q15, Q16, Q17, Q18, Q19, Q20, Q21, Q22, Q23, Q24, Q25, Q26, Q27, Q28, Q29, Q30, Q31, Q32, Q33]), "operationType" : NewBodyOperationType.REMOVE, "oppositeDirection" : true, "depth" : .5 * mm});
        }
    });
